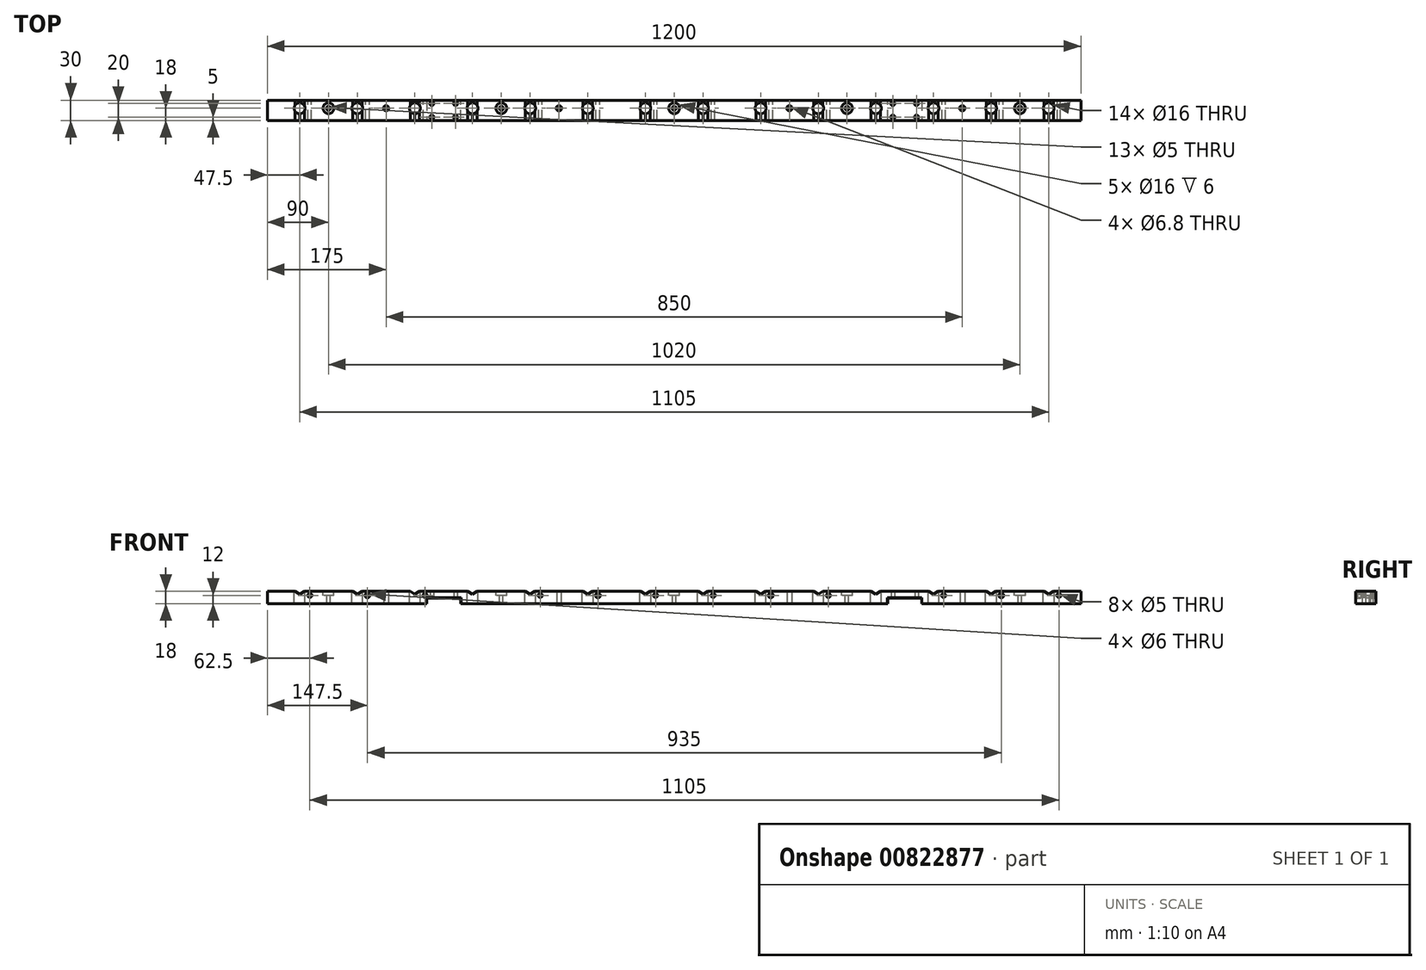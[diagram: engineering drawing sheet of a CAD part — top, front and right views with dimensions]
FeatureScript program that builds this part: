
annotation { "Feature Type Name" : "Feature", "Feature Type Description" : "" }
export const myFeature = defineFeature(function(context is Context, id is Id, definition is map)
    precondition{}
    {
        {
            var Q0;
            Q0=qCreatedBy(makeId("Front.planeOp"),FACE);
            var sketch = newSketch(context, id + "F0", { "sketchPlane" : qUnion([Q0])});
            skLineSegment(sketch, "E0.bottom", {"start": v(-600, -9) * mm, "end": v(600, -9) * mm});
            skLineSegment(sketch, "E0.top", {"start": v(-600, 9) * mm, "end": v(-559.43, 9) * mm});
            skLineSegment(sketch, "E0.left", {"start": v(-600, -9) * mm, "end": v(-600, 9) * mm});
            skLineSegment(sketch, "E0.right", {"start": v(600, -9) * mm, "end": v(600, 9) * mm});
            skPoint(sketch, "E0.middle", {"position": v(0, 0) * mm});
            skLineSegment(sketch, "E1", {"start": v(0, 0) * mm, "end": v(0, 102.74) * mm, "construction": true});
            skLineSegment(sketch, "E2", {"start": v(0, 102.74) * mm, "end": v(-552.5, 102.74) * mm, "construction": true});
            skLineSegment(sketch, "E3", {"start": v(-552.5, 102.74) * mm, "end": v(-552.5, -48.6) * mm, "construction": true});
            skLineSegment(sketch, "E4", {"start": v(-552.5, 5) * mm, "end": v(-545.57, 9) * mm});
            skLineSegment(sketch, "E5.MirrorCS", {"start": v(-552.5, 5) * mm, "end": v(-559.43, 9) * mm});
            skLineSegment(sketch, "E6.1.0.0", {"start": v(-467.5, 5) * mm, "end": v(-460.57, 9) * mm});
            skLineSegment(sketch, "E6.1.0.1", {"start": v(-467.5, 5) * mm, "end": v(-474.43, 9) * mm});
            skLineSegment(sketch, "E6.2.0.0", {"start": v(-382.5, 5) * mm, "end": v(-375.57, 9) * mm});
            skLineSegment(sketch, "E6.2.0.1", {"start": v(-382.5, 5) * mm, "end": v(-389.43, 9) * mm});
            skLineSegment(sketch, "E6.3.0.0", {"start": v(-297.5, 5) * mm, "end": v(-290.57, 9) * mm});
            skLineSegment(sketch, "E6.3.0.1", {"start": v(-297.5, 5) * mm, "end": v(-304.43, 9) * mm});
            skLineSegment(sketch, "E6.4.0.0", {"start": v(-212.5, 5) * mm, "end": v(-205.57, 9) * mm});
            skLineSegment(sketch, "E6.4.0.1", {"start": v(-212.5, 5) * mm, "end": v(-219.43, 9) * mm});
            skLineSegment(sketch, "E6.5.0.0", {"start": v(-127.5, 5) * mm, "end": v(-120.57, 9) * mm});
            skLineSegment(sketch, "E6.5.0.1", {"start": v(-127.5, 5) * mm, "end": v(-134.43, 9) * mm});
            skLineSegment(sketch, "E6.6.0.0", {"start": v(-42.5, 5) * mm, "end": v(-35.57, 9) * mm});
            skLineSegment(sketch, "E6.6.0.1", {"start": v(-42.5, 5) * mm, "end": v(-49.43, 9) * mm});
            skLineSegment(sketch, "E6.7.0.0", {"start": v(42.5, 5) * mm, "end": v(49.43, 9) * mm});
            skLineSegment(sketch, "E6.7.0.1", {"start": v(42.5, 5) * mm, "end": v(35.57, 9) * mm});
            skLineSegment(sketch, "E6.8.0.0", {"start": v(127.5, 5) * mm, "end": v(134.43, 9) * mm});
            skLineSegment(sketch, "E6.8.0.1", {"start": v(127.5, 5) * mm, "end": v(120.57, 9) * mm});
            skLineSegment(sketch, "E6.9.0.0", {"start": v(212.5, 5) * mm, "end": v(219.43, 9) * mm});
            skLineSegment(sketch, "E6.9.0.1", {"start": v(212.5, 5) * mm, "end": v(205.57, 9) * mm});
            skLineSegment(sketch, "E6.10.0.0", {"start": v(297.5, 5) * mm, "end": v(304.43, 9) * mm});
            skLineSegment(sketch, "E6.10.0.1", {"start": v(297.5, 5) * mm, "end": v(290.57, 9) * mm});
            skLineSegment(sketch, "E6.11.0.0", {"start": v(382.5, 5) * mm, "end": v(389.43, 9) * mm});
            skLineSegment(sketch, "E6.11.0.1", {"start": v(382.5, 5) * mm, "end": v(375.57, 9) * mm});
            skLineSegment(sketch, "E6.12.0.0", {"start": v(467.5, 5) * mm, "end": v(474.43, 9) * mm});
            skLineSegment(sketch, "E6.12.0.1", {"start": v(467.5, 5) * mm, "end": v(460.57, 9) * mm});
            skLineSegment(sketch, "E6.13.0.0", {"start": v(552.5, 5) * mm, "end": v(559.43, 9) * mm});
            skLineSegment(sketch, "E6.13.0.1", {"start": v(552.5, 5) * mm, "end": v(545.57, 9) * mm});
            skLineSegment(sketch, "E7.trimOffspring", {"start": v(-545.57, 9) * mm, "end": v(-474.43, 9) * mm, "construction": true});
            skLineSegment(sketch, "E8.trimOffspring", {"start": v(-460.57, 9) * mm, "end": v(-389.43, 9) * mm});
            skLineSegment(sketch, "E9.trimOffspring", {"start": v(-545.57, 9) * mm, "end": v(-474.43, 9) * mm});
            skLineSegment(sketch, "E10.trimOffspring", {"start": v(-375.57, 9) * mm, "end": v(-304.43, 9) * mm});
            skLineSegment(sketch, "E11.trimOffspring", {"start": v(-290.57, 9) * mm, "end": v(-219.43, 9) * mm});
            skLineSegment(sketch, "E12.trimOffspring", {"start": v(-205.57, 9) * mm, "end": v(-134.43, 9) * mm});
            skLineSegment(sketch, "E13.trimOffspring", {"start": v(-120.57, 9) * mm, "end": v(-49.43, 9) * mm});
            skLineSegment(sketch, "E14.trimOffspring", {"start": v(-35.57, 9) * mm, "end": v(35.57, 9) * mm});
            skLineSegment(sketch, "E15.trimOffspring", {"start": v(49.43, 9) * mm, "end": v(120.57, 9) * mm});
            skLineSegment(sketch, "E16.trimOffspring", {"start": v(134.43, 9) * mm, "end": v(205.57, 9) * mm});
            skLineSegment(sketch, "E17.trimOffspring", {"start": v(219.43, 9) * mm, "end": v(290.57, 9) * mm});
            skLineSegment(sketch, "E18.trimOffspring", {"start": v(304.43, 9) * mm, "end": v(375.57, 9) * mm});
            skLineSegment(sketch, "E19.trimOffspring", {"start": v(389.43, 9) * mm, "end": v(460.57, 9) * mm});
            skLineSegment(sketch, "E20.trimOffspring", {"start": v(474.43, 9) * mm, "end": v(545.57, 9) * mm});
            skLineSegment(sketch, "E21.trimOffspring", {"start": v(559.43, 9) * mm, "end": v(600, 9) * mm});
            skSolve(sketch);
        }
        {
            var Q0;
            Q0 = qSketchRegion(id + "F0", true);
            extrude(context, id + "F1", {"entities" : qUnion([Q0]), "endBound" : BoundingType.SYMMETRIC, "depth" : 24 * mm, "offsetDistance" : 25 * mm});
        }
        {
            var Q0;
            Q0=qCreatedBy(makeId("Top.planeOp"),FACE);
            var sketch = newSketch(context, id + "F2", { "sketchPlane" : qUnion([Q0])});
            skLineSegment(sketch, "E22", {"start": v(0, 0) * mm, "end": v(0, 120.86) * mm, "construction": true});
            skLineSegment(sketch, "E23", {"start": v(0, 120.86) * mm, "end": v(-552.5, 120.86) * mm, "construction": true});
            skLineSegment(sketch, "E24", {"start": v(-552.5, 120.86) * mm, "end": v(-552.5, 0) * mm, "construction": true});
            skLineSegment(sketch, "E25", {"start": v(0, 0) * mm, "end": v(-552.5, 0) * mm, "construction": true});
            skCircle(sketch, "E26", {"center": v(-552.5, 0) * mm, "radius": 8 * mm});
            skCircle(sketch, "E27.1.0.0", {"center": v(-467.5, 0) * mm, "radius": 8 * mm});
            skCircle(sketch, "E27.2.0.0", {"center": v(-382.5, 0) * mm, "radius": 8 * mm});
            skCircle(sketch, "E27.3.0.0", {"center": v(-297.5, 0) * mm, "radius": 8 * mm});
            skCircle(sketch, "E27.4.0.0", {"center": v(-212.5, 0) * mm, "radius": 8 * mm});
            skCircle(sketch, "E27.5.0.0", {"center": v(-127.5, 0) * mm, "radius": 8 * mm});
            skCircle(sketch, "E27.6.0.0", {"center": v(-42.5, 0) * mm, "radius": 8 * mm});
            skCircle(sketch, "E27.7.0.0", {"center": v(42.5, 0) * mm, "radius": 8 * mm});
            skCircle(sketch, "E27.8.0.0", {"center": v(127.5, 0) * mm, "radius": 8 * mm});
            skCircle(sketch, "E27.9.0.0", {"center": v(212.5, 0) * mm, "radius": 8 * mm});
            skCircle(sketch, "E27.10.0.0", {"center": v(297.5, 0) * mm, "radius": 8 * mm});
            skCircle(sketch, "E27.11.0.0", {"center": v(382.5, 0) * mm, "radius": 8 * mm});
            skCircle(sketch, "E27.12.0.0", {"center": v(467.5, 0) * mm, "radius": 8 * mm});
            skCircle(sketch, "E27.13.0.0", {"center": v(552.5, 0) * mm, "radius": 8 * mm});
            skLineSegment(sketch, "E27.direction1", {"start": v(-552.5, 0) * mm, "end": v(-467.5, 0) * mm, "construction": true});
            skSolve(sketch);
        }
        {
            var Q0;
            Q0 = qSketchRegion(id + "F2", true);
            extrude(context, id + "F3", {"entities" : qUnion([Q0]), "operationType" : NewBodyOperationType.REMOVE, "endBound" : BoundingType.SYMMETRIC, "oppositeDirection" : true, "depth" : 25 * mm, "offsetDistance" : 25 * mm});
        }
        {
            var Q0;
            Q0=makeQuery(id+"F1.opExtrude","CAP_FACE",FACE,{"disambiguationData":[OSD([sQuery(id+"F0.wireOp",EDGE,"E0.bottom"),sQuery(id+"F0.wireOp",EDGE,"E0.top"),sQuery(id+"F0.wireOp",EDGE,"E0.left"),sQuery(id+"F0.wireOp",EDGE,"E0.right"),sQuery(id+"F0.wireOp",EDGE,"E4"),sQuery(id+"F0.wireOp",EDGE,"E5.MirrorCS"),sQuery(id+"F0.wireOp",EDGE,"E6.1.0.0"),sQuery(id+"F0.wireOp",EDGE,"E6.1.0.1"),sQuery(id+"F0.wireOp",EDGE,"E6.2.0.0"),sQuery(id+"F0.wireOp",EDGE,"E6.2.0.1"),sQuery(id+"F0.wireOp",EDGE,"E6.3.0.0"),sQuery(id+"F0.wireOp",EDGE,"E6.3.0.1"),sQuery(id+"F0.wireOp",EDGE,"E6.4.0.0"),sQuery(id+"F0.wireOp",EDGE,"E6.4.0.1"),sQuery(id+"F0.wireOp",EDGE,"E6.5.0.0"),sQuery(id+"F0.wireOp",EDGE,"E6.5.0.1"),sQuery(id+"F0.wireOp",EDGE,"E6.6.0.0"),sQuery(id+"F0.wireOp",EDGE,"E6.6.0.1"),sQuery(id+"F0.wireOp",EDGE,"E6.7.0.0"),sQuery(id+"F0.wireOp",EDGE,"E6.7.0.1"),sQuery(id+"F0.wireOp",EDGE,"E6.8.0.0"),sQuery(id+"F0.wireOp",EDGE,"E6.8.0.1"),sQuery(id+"F0.wireOp",EDGE,"E6.9.0.0"),sQuery(id+"F0.wireOp",EDGE,"E6.9.0.1"),sQuery(id+"F0.wireOp",EDGE,"E6.10.0.0"),sQuery(id+"F0.wireOp",EDGE,"E6.10.0.1"),sQuery(id+"F0.wireOp",EDGE,"E6.11.0.0"),sQuery(id+"F0.wireOp",EDGE,"E6.11.0.1"),sQuery(id+"F0.wireOp",EDGE,"E6.12.0.0"),sQuery(id+"F0.wireOp",EDGE,"E6.12.0.1"),sQuery(id+"F0.wireOp",EDGE,"E6.13.0.0"),sQuery(id+"F0.wireOp",EDGE,"E6.13.0.1"),sQuery(id+"F0.wireOp",EDGE,"E8.trimOffspring"),sQuery(id+"F0.wireOp",EDGE,"E9.trimOffspring"),sQuery(id+"F0.wireOp",EDGE,"E10.trimOffspring"),sQuery(id+"F0.wireOp",EDGE,"E11.trimOffspring"),sQuery(id+"F0.wireOp",EDGE,"E12.trimOffspring"),sQuery(id+"F0.wireOp",EDGE,"E13.trimOffspring"),sQuery(id+"F0.wireOp",EDGE,"E14.trimOffspring"),sQuery(id+"F0.wireOp",EDGE,"E15.trimOffspring"),sQuery(id+"F0.wireOp",EDGE,"E16.trimOffspring"),sQuery(id+"F0.wireOp",EDGE,"E17.trimOffspring"),sQuery(id+"F0.wireOp",EDGE,"E18.trimOffspring"),sQuery(id+"F0.wireOp",EDGE,"E19.trimOffspring"),sQuery(id+"F0.wireOp",EDGE,"E20.trimOffspring"),sQuery(id+"F0.wireOp",EDGE,"E21.trimOffspring")])],"isStart":false});
            extrude(context, id + "F4", {"entities" : qUnion([Q0]), "operationType" : NewBodyOperationType.ADD, "depth" : 6 * mm, "offsetDistance" : 25 * mm});
        }
        {
            var Q0;
            Q0=makeQuery(id+"F1.opExtrude","CAP_FACE",FACE,{"disambiguationData":[OSD([sQuery(id+"F0.wireOp",EDGE,"E0.bottom"),sQuery(id+"F0.wireOp",EDGE,"E0.top"),sQuery(id+"F0.wireOp",EDGE,"E0.left"),sQuery(id+"F0.wireOp",EDGE,"E0.right"),sQuery(id+"F0.wireOp",EDGE,"E4"),sQuery(id+"F0.wireOp",EDGE,"E5.MirrorCS"),sQuery(id+"F0.wireOp",EDGE,"E6.1.0.0"),sQuery(id+"F0.wireOp",EDGE,"E6.1.0.1"),sQuery(id+"F0.wireOp",EDGE,"E6.2.0.0"),sQuery(id+"F0.wireOp",EDGE,"E6.2.0.1"),sQuery(id+"F0.wireOp",EDGE,"E6.3.0.0"),sQuery(id+"F0.wireOp",EDGE,"E6.3.0.1"),sQuery(id+"F0.wireOp",EDGE,"E6.4.0.0"),sQuery(id+"F0.wireOp",EDGE,"E6.4.0.1"),sQuery(id+"F0.wireOp",EDGE,"E6.5.0.0"),sQuery(id+"F0.wireOp",EDGE,"E6.5.0.1"),sQuery(id+"F0.wireOp",EDGE,"E6.6.0.0"),sQuery(id+"F0.wireOp",EDGE,"E6.6.0.1"),sQuery(id+"F0.wireOp",EDGE,"E6.7.0.0"),sQuery(id+"F0.wireOp",EDGE,"E6.7.0.1"),sQuery(id+"F0.wireOp",EDGE,"E6.8.0.0"),sQuery(id+"F0.wireOp",EDGE,"E6.8.0.1"),sQuery(id+"F0.wireOp",EDGE,"E6.9.0.0"),sQuery(id+"F0.wireOp",EDGE,"E6.9.0.1"),sQuery(id+"F0.wireOp",EDGE,"E6.10.0.0"),sQuery(id+"F0.wireOp",EDGE,"E6.10.0.1"),sQuery(id+"F0.wireOp",EDGE,"E6.11.0.0"),sQuery(id+"F0.wireOp",EDGE,"E6.11.0.1"),sQuery(id+"F0.wireOp",EDGE,"E6.12.0.0"),sQuery(id+"F0.wireOp",EDGE,"E6.12.0.1"),sQuery(id+"F0.wireOp",EDGE,"E6.13.0.0"),sQuery(id+"F0.wireOp",EDGE,"E6.13.0.1"),sQuery(id+"F0.wireOp",EDGE,"E8.trimOffspring"),sQuery(id+"F0.wireOp",EDGE,"E9.trimOffspring"),sQuery(id+"F0.wireOp",EDGE,"E10.trimOffspring"),sQuery(id+"F0.wireOp",EDGE,"E11.trimOffspring"),sQuery(id+"F0.wireOp",EDGE,"E12.trimOffspring"),sQuery(id+"F0.wireOp",EDGE,"E13.trimOffspring"),sQuery(id+"F0.wireOp",EDGE,"E14.trimOffspring"),sQuery(id+"F0.wireOp",EDGE,"E15.trimOffspring"),sQuery(id+"F0.wireOp",EDGE,"E16.trimOffspring"),sQuery(id+"F0.wireOp",EDGE,"E17.trimOffspring"),sQuery(id+"F0.wireOp",EDGE,"E18.trimOffspring"),sQuery(id+"F0.wireOp",EDGE,"E19.trimOffspring"),sQuery(id+"F0.wireOp",EDGE,"E20.trimOffspring"),sQuery(id+"F0.wireOp",EDGE,"E21.trimOffspring")])],"isStart":true});
            var sketch = newSketch(context, id + "F5", { "sketchPlane" : qUnion([Q0])});
            skLineSegment(sketch, "E28.0", {"start": v(-559.43, 9) * mm, "end": v(-600, 9) * mm, "construction": true});
            skLineSegment(sketch, "E29", {"start": v(-631.78, 3) * mm, "end": v(-527.52, 3) * mm, "construction": true});
            skLineSegment(sketch, "E30", {"start": v(-527.52, 3) * mm, "end": v(-567.5, 61.8) * mm, "construction": true});
            skLineSegment(sketch, "E31", {"start": v(-567.5, 61.8) * mm, "end": v(-567.5, -52.53) * mm, "construction": true});
            skCircle(sketch, "E32", {"center": v(-567.5, 3) * mm, "radius": 2.5 * mm});
            skCircle(sketch, "E33.1.0.0", {"center": v(-482.5, 3) * mm, "radius": 2.5 * mm, "construction": true});
            skCircle(sketch, "E33.2.0.0", {"center": v(-397.5, 3) * mm, "radius": 2.5 * mm});
            skCircle(sketch, "E33.3.0.0", {"center": v(-312.5, 3) * mm, "radius": 2.5 * mm, "construction": true});
            skCircle(sketch, "E33.4.0.0", {"center": v(-227.5, 3) * mm, "radius": 2.5 * mm});
            skCircle(sketch, "E33.5.0.0", {"center": v(-142.5, 3) * mm, "radius": 2.5 * mm, "construction": true});
            skCircle(sketch, "E33.6.0.0", {"center": v(-57.5, 3) * mm, "radius": 2.5 * mm});
            skCircle(sketch, "E33.7.0.0", {"center": v(27.5, 3) * mm, "radius": 2.5 * mm});
            skCircle(sketch, "E33.8.0.0", {"center": v(112.5, 3) * mm, "radius": 2.5 * mm, "construction": true});
            skCircle(sketch, "E33.9.0.0", {"center": v(197.5, 3) * mm, "radius": 2.5 * mm});
            skCircle(sketch, "E33.10.0.0", {"center": v(282.5, 3) * mm, "radius": 2.5 * mm, "construction": true});
            skCircle(sketch, "E33.11.0.0", {"center": v(367.5, 3) * mm, "radius": 2.5 * mm});
            skCircle(sketch, "E33.12.0.0", {"center": v(452.5, 3) * mm, "radius": 2.5 * mm, "construction": true});
            skCircle(sketch, "E33.13.0.0", {"center": v(537.5, 3) * mm, "radius": 2.5 * mm});
            skLineSegment(sketch, "E33.direction1", {"start": v(-567.5, 3) * mm, "end": v(-482.5, 3) * mm, "construction": true});
            skSolve(sketch);
        }
        {
            var Q0;
            Q0 = qSketchRegion(id + "F5", true);
            extrude(context, id + "F6", {"entities" : qUnion([Q0]), "operationType" : NewBodyOperationType.REMOVE, "endBound" : BoundingType.UP_TO_NEXT, "oppositeDirection" : true, "depth" : 15 * mm, "offsetDistance" : 25 * mm});
        }
        {
            var Q0;
            Q0=makeQuery(id+"F5.imprint","IMPRINT",FACE,{"disambiguationData":[TD([[makeQuery(id+"F5.imprint","IMPRINT",EDGE,{"derivedFrom":sQuery(id+"F5.wireOp",EDGE,"E32")}),-1.0]])]});
            var sketch = newSketch(context, id + "F7", { "sketchPlane" : qUnion([Q0])});
            skCircle(sketch, "E34.0", {"center": v(-482.5, 3) * mm, "radius": 2.5 * mm, "construction": true});
            skCircle(sketch, "E35.0", {"center": v(-142.5, 3) * mm, "radius": 2.5 * mm, "construction": true});
            skCircle(sketch, "E36.0", {"center": v(112.5, 3) * mm, "radius": 2.5 * mm, "construction": true});
            skCircle(sketch, "E37.0", {"center": v(452.5, 3) * mm, "radius": 2.5 * mm, "construction": true});
            skCircle(sketch, "E38", {"center": v(-482.5, 3) * mm, "radius": 3 * mm});
            skCircle(sketch, "E39", {"center": v(-142.5, 3) * mm, "radius": 3 * mm});
            skCircle(sketch, "E40", {"center": v(112.5, 3) * mm, "radius": 3 * mm});
            skCircle(sketch, "E41", {"center": v(452.5, 3) * mm, "radius": 3 * mm});
            skSolve(sketch);
        }
        {
            var Q0;
            Q0 = qSketchRegion(id + "F7", true);
            extrude(context, id + "F8", {"entities" : qUnion([Q0]), "operationType" : NewBodyOperationType.REMOVE, "endBound" : BoundingType.UP_TO_NEXT, "oppositeDirection" : true, "depth" : 25 * mm, "offsetDistance" : 25 * mm});
        }
        {
            var Q0;
            Q0=makeQuery(id+"F6.boolean.opBoolean","COPY",FACE,{"derivedFrom":makeQuery(id+"F6.opExtrude","SWEPT_FACE",FACE,{"disambiguationData":[OSD([sQuery(id+"F5.wireOp",EDGE,"E32")])]})});
            var Q1;
            Q1=makeQuery(id+"F8.boolean.opBoolean","COPY",FACE,{"derivedFrom":makeQuery(id+"F8.opExtrude","SWEPT_FACE",FACE,{"disambiguationData":[OSD([sQuery(id+"F7.wireOp",EDGE,"E38")])]})});
            var Q2;
            Q2=makeQuery(id+"F6.boolean.opBoolean","COPY",FACE,{"derivedFrom":makeQuery(id+"F6.opExtrude","SWEPT_FACE",FACE,{"disambiguationData":[OSD([sQuery(id+"F5.wireOp",EDGE,"E33.2.0.0")])]})});
            var Q3;
            Q3=makeQuery(id+"F6.boolean.opBoolean","COPY",FACE,{"derivedFrom":makeQuery(id+"F6.opExtrude","SWEPT_FACE",FACE,{"disambiguationData":[OSD([sQuery(id+"F5.wireOp",EDGE,"E33.4.0.0")])]})});
            var Q4;
            Q4=makeQuery(id+"F8.boolean.opBoolean","COPY",FACE,{"derivedFrom":makeQuery(id+"F8.opExtrude","SWEPT_FACE",FACE,{"disambiguationData":[OSD([sQuery(id+"F7.wireOp",EDGE,"E39")])]})});
            var Q5;
            Q5=makeQuery(id+"F6.boolean.opBoolean","COPY",FACE,{"derivedFrom":makeQuery(id+"F6.opExtrude","SWEPT_FACE",FACE,{"disambiguationData":[OSD([sQuery(id+"F5.wireOp",EDGE,"E33.6.0.0")])]})});
            var Q6;
            Q6=makeQuery(id+"F6.boolean.opBoolean","COPY",FACE,{"derivedFrom":makeQuery(id+"F6.opExtrude","SWEPT_FACE",FACE,{"disambiguationData":[OSD([sQuery(id+"F5.wireOp",EDGE,"E33.7.0.0")])]})});
            var Q7;
            Q7=makeQuery(id+"F8.boolean.opBoolean","COPY",FACE,{"derivedFrom":makeQuery(id+"F8.opExtrude","SWEPT_FACE",FACE,{"disambiguationData":[OSD([sQuery(id+"F7.wireOp",EDGE,"E40")])]})});
            var Q8;
            Q8=makeQuery(id+"F6.boolean.opBoolean","COPY",FACE,{"derivedFrom":makeQuery(id+"F6.opExtrude","SWEPT_FACE",FACE,{"disambiguationData":[OSD([sQuery(id+"F5.wireOp",EDGE,"E33.9.0.0")])]})});
            var Q9;
            Q9=makeQuery(id+"F6.boolean.opBoolean","COPY",FACE,{"derivedFrom":makeQuery(id+"F6.opExtrude","SWEPT_FACE",FACE,{"disambiguationData":[OSD([sQuery(id+"F5.wireOp",EDGE,"E33.11.0.0")])]})});
            var Q10;
            Q10=makeQuery(id+"F8.boolean.opBoolean","COPY",FACE,{"derivedFrom":makeQuery(id+"F8.opExtrude","SWEPT_FACE",FACE,{"disambiguationData":[OSD([sQuery(id+"F7.wireOp",EDGE,"E41")])]})});
            var Q11;
            Q11=makeQuery(id+"F6.boolean.opBoolean","COPY",FACE,{"derivedFrom":makeQuery(id+"F6.opExtrude","SWEPT_FACE",FACE,{"disambiguationData":[OSD([sQuery(id+"F5.wireOp",EDGE,"E33.13.0.0")])]})});
            var Q12;
            Q12=makeQuery(id+"F3.boolean.opBoolean","INTERSECT",EDGE,{"derivedFrom":[makeQuery(id+"F1.opExtrude","SWEPT_FACE",FACE,{"disambiguationData":[OSD([sQuery(id+"F0.wireOp",EDGE,"E0.bottom")])]}),makeQuery(id+"F3.opExtrude","SWEPT_FACE",FACE,{"disambiguationData":[OSD([sQuery(id+"F2.wireOp",EDGE,"E26")])]})]});
            var Q13;
            Q13=makeQuery(id+"F3.boolean.opBoolean","INTERSECT",EDGE,{"derivedFrom":[makeQuery(id+"F1.opExtrude","SWEPT_FACE",FACE,{"disambiguationData":[OSD([sQuery(id+"F0.wireOp",EDGE,"E0.bottom")])]}),makeQuery(id+"F3.opExtrude","SWEPT_FACE",FACE,{"disambiguationData":[OSD([sQuery(id+"F2.wireOp",EDGE,"E27.1.0.0")])]})]});
            var Q14;
            Q14=makeQuery(id+"F3.boolean.opBoolean","INTERSECT",EDGE,{"derivedFrom":[makeQuery(id+"F1.opExtrude","SWEPT_FACE",FACE,{"disambiguationData":[OSD([sQuery(id+"F0.wireOp",EDGE,"E0.bottom")])]}),makeQuery(id+"F3.opExtrude","SWEPT_FACE",FACE,{"disambiguationData":[OSD([sQuery(id+"F2.wireOp",EDGE,"E27.2.0.0")])]})]});
            var Q15;
            Q15=makeQuery(id+"F3.boolean.opBoolean","INTERSECT",EDGE,{"derivedFrom":[makeQuery(id+"F1.opExtrude","SWEPT_FACE",FACE,{"disambiguationData":[OSD([sQuery(id+"F0.wireOp",EDGE,"E0.bottom")])]}),makeQuery(id+"F3.opExtrude","SWEPT_FACE",FACE,{"disambiguationData":[OSD([sQuery(id+"F2.wireOp",EDGE,"E27.3.0.0")])]})]});
            var Q16;
            Q16=makeQuery(id+"F3.boolean.opBoolean","INTERSECT",EDGE,{"derivedFrom":[makeQuery(id+"F1.opExtrude","SWEPT_FACE",FACE,{"disambiguationData":[OSD([sQuery(id+"F0.wireOp",EDGE,"E0.bottom")])]}),makeQuery(id+"F3.opExtrude","SWEPT_FACE",FACE,{"disambiguationData":[OSD([sQuery(id+"F2.wireOp",EDGE,"E27.4.0.0")])]})]});
            var Q17;
            Q17=makeQuery(id+"F3.boolean.opBoolean","INTERSECT",EDGE,{"derivedFrom":[makeQuery(id+"F1.opExtrude","SWEPT_FACE",FACE,{"disambiguationData":[OSD([sQuery(id+"F0.wireOp",EDGE,"E0.bottom")])]}),makeQuery(id+"F3.opExtrude","SWEPT_FACE",FACE,{"disambiguationData":[OSD([sQuery(id+"F2.wireOp",EDGE,"E27.5.0.0")])]})]});
            var Q18;
            Q18=makeQuery(id+"F3.boolean.opBoolean","INTERSECT",EDGE,{"derivedFrom":[makeQuery(id+"F1.opExtrude","SWEPT_FACE",FACE,{"disambiguationData":[OSD([sQuery(id+"F0.wireOp",EDGE,"E0.bottom")])]}),makeQuery(id+"F3.opExtrude","SWEPT_FACE",FACE,{"disambiguationData":[OSD([sQuery(id+"F2.wireOp",EDGE,"E27.6.0.0")])]})]});
            var Q19;
            Q19=makeQuery(id+"F3.boolean.opBoolean","INTERSECT",EDGE,{"derivedFrom":[makeQuery(id+"F1.opExtrude","SWEPT_FACE",FACE,{"disambiguationData":[OSD([sQuery(id+"F0.wireOp",EDGE,"E0.bottom")])]}),makeQuery(id+"F3.opExtrude","SWEPT_FACE",FACE,{"disambiguationData":[OSD([sQuery(id+"F2.wireOp",EDGE,"E27.7.0.0")])]})]});
            var Q20;
            Q20=makeQuery(id+"F3.boolean.opBoolean","INTERSECT",EDGE,{"derivedFrom":[makeQuery(id+"F1.opExtrude","SWEPT_FACE",FACE,{"disambiguationData":[OSD([sQuery(id+"F0.wireOp",EDGE,"E0.bottom")])]}),makeQuery(id+"F3.opExtrude","SWEPT_FACE",FACE,{"disambiguationData":[OSD([sQuery(id+"F2.wireOp",EDGE,"E27.8.0.0")])]})]});
            var Q21;
            Q21=makeQuery(id+"F3.boolean.opBoolean","INTERSECT",EDGE,{"derivedFrom":[makeQuery(id+"F1.opExtrude","SWEPT_FACE",FACE,{"disambiguationData":[OSD([sQuery(id+"F0.wireOp",EDGE,"E0.bottom")])]}),makeQuery(id+"F3.opExtrude","SWEPT_FACE",FACE,{"disambiguationData":[OSD([sQuery(id+"F2.wireOp",EDGE,"E27.9.0.0")])]})]});
            var Q22;
            Q22=makeQuery(id+"F3.boolean.opBoolean","INTERSECT",EDGE,{"derivedFrom":[makeQuery(id+"F1.opExtrude","SWEPT_FACE",FACE,{"disambiguationData":[OSD([sQuery(id+"F0.wireOp",EDGE,"E0.bottom")])]}),makeQuery(id+"F3.opExtrude","SWEPT_FACE",FACE,{"disambiguationData":[OSD([sQuery(id+"F2.wireOp",EDGE,"E27.10.0.0")])]})]});
            var Q23;
            Q23=makeQuery(id+"F3.boolean.opBoolean","INTERSECT",EDGE,{"derivedFrom":[makeQuery(id+"F1.opExtrude","SWEPT_FACE",FACE,{"disambiguationData":[OSD([sQuery(id+"F0.wireOp",EDGE,"E0.bottom")])]}),makeQuery(id+"F3.opExtrude","SWEPT_FACE",FACE,{"disambiguationData":[OSD([sQuery(id+"F2.wireOp",EDGE,"E27.11.0.0")])]})]});
            var Q24;
            Q24=makeQuery(id+"F3.boolean.opBoolean","INTERSECT",EDGE,{"derivedFrom":[makeQuery(id+"F1.opExtrude","SWEPT_FACE",FACE,{"disambiguationData":[OSD([sQuery(id+"F0.wireOp",EDGE,"E0.bottom")])]}),makeQuery(id+"F3.opExtrude","SWEPT_FACE",FACE,{"disambiguationData":[OSD([sQuery(id+"F2.wireOp",EDGE,"E27.12.0.0")])]})]});
            var Q25;
            Q25=makeQuery(id+"F3.boolean.opBoolean","INTERSECT",EDGE,{"derivedFrom":[makeQuery(id+"F1.opExtrude","SWEPT_FACE",FACE,{"disambiguationData":[OSD([sQuery(id+"F0.wireOp",EDGE,"E0.bottom")])]}),makeQuery(id+"F3.opExtrude","SWEPT_FACE",FACE,{"disambiguationData":[OSD([sQuery(id+"F2.wireOp",EDGE,"E27.13.0.0")])]})]});
            chamfer(context, id + "F9", {"entities" : qUnion([Q0, Q1, Q2, Q3, Q4, Q5, Q6, Q7, Q8, Q9, Q10, Q11, Q12, Q13, Q14, Q15, Q16, Q17, Q18, Q19, Q20, Q21, Q22, Q23, Q24, Q25]), "width" : 0.5 * mm, "tangentPropagation" : true});
        }
        {
            var Q0;
            Q0=qCreatedBy(makeId("Top.planeOp"),FACE);
            var sketch = newSketch(context, id + "F10", { "sketchPlane" : qUnion([Q0])});
            skLineSegment(sketch, "E42", {"start": v(0, 0) * mm, "end": v(-510, 0) * mm, "construction": true});
            skCircle(sketch, "E43", {"center": v(-510, 0) * mm, "radius": 2.5 * mm});
            skCircle(sketch, "E44", {"center": v(-510, 0) * mm, "radius": 8 * mm, "construction": true});
            skCircle(sketch, "E45.1.0.0", {"center": v(-255, 0) * mm, "radius": 2.5 * mm});
            skCircle(sketch, "E45.2.0.0", {"center": v(0, 0) * mm, "radius": 2.5 * mm});
            skCircle(sketch, "E45.3.0.0", {"center": v(255, 0) * mm, "radius": 2.5 * mm});
            skCircle(sketch, "E45.4.0.0", {"center": v(510, 0) * mm, "radius": 2.5 * mm});
            skLineSegment(sketch, "E45.direction1", {"start": v(-510, 0) * mm, "end": v(-255, 0) * mm, "construction": true});
            skSolve(sketch);
        }
        {
            var Q0;
            Q0 = qSketchRegion(id + "F10", true);
            extrude(context, id + "F11", {"entities" : qUnion([Q0]), "operationType" : NewBodyOperationType.REMOVE, "endBound" : BoundingType.SYMMETRIC, "oppositeDirection" : true, "depth" : 25 * mm, "offsetDistance" : 25 * mm});
        }
        {
            var Q0;
            {var subQ0=sQuery(id+"F0.wireOp",EDGE,"E9.trimOffspring");Q0=makeQuery(id+"F4.boolean.opBoolean","MERGE",FACE,{"derivedFrom":[makeQuery(id+"F1.opExtrude","SWEPT_FACE",FACE,{"disambiguationData":[OSD([subQ0])]}),makeQuery(id+"F4.opExtrude","SWEPT_FACE",FACE,{"disambiguationData":[OSD([subQ0])]})]});}
            var sketch = newSketch(context, id + "F12", { "sketchPlane" : qUnion([Q0])});
            skCircle(sketch, "E46.0", {"center": v(-510, 0) * mm, "radius": 2.5 * mm, "construction": true});
            skCircle(sketch, "E47.0", {"center": v(-255, 0) * mm, "radius": 2.5 * mm, "construction": true});
            skCircle(sketch, "E48.0", {"center": v(0, 0) * mm, "radius": 2.5 * mm, "construction": true});
            skCircle(sketch, "E49.0", {"center": v(255, 0) * mm, "radius": 2.5 * mm, "construction": true});
            skCircle(sketch, "E50.0", {"center": v(510, 0) * mm, "radius": 2.5 * mm, "construction": true});
            skCircle(sketch, "E51", {"center": v(-510, 0) * mm, "radius": 8 * mm});
            skCircle(sketch, "E52.1.0.0", {"center": v(-255, 0) * mm, "radius": 8 * mm});
            skCircle(sketch, "E52.2.0.0", {"center": v(0, 0) * mm, "radius": 8 * mm});
            skCircle(sketch, "E52.3.0.0", {"center": v(255, 0) * mm, "radius": 8 * mm});
            skCircle(sketch, "E52.4.0.0", {"center": v(510, 0) * mm, "radius": 8 * mm});
            skLineSegment(sketch, "E52.direction1", {"start": v(-510, 0) * mm, "end": v(-255, 0) * mm, "construction": true});
            skSolve(sketch);
        }
        {
            var Q0;
            Q0 = qSketchRegion(id + "F12", true);
            extrude(context, id + "F13", {"entities" : qUnion([Q0]), "operationType" : NewBodyOperationType.REMOVE, "oppositeDirection" : true, "depth" : 6 * mm, "offsetDistance" : 25 * mm});
        }
        {
            var Q0;
            Q0=makeQuery(id+"F13.boolean.opBoolean","COPY",EDGE,{"derivedFrom":makeQuery(id+"F13.opExtrude","CAP_EDGE",EDGE,{"disambiguationData":[OSD([sQuery(id+"F12.wireOp",EDGE,"E52.3.0.0")])],"isStart":true})});
            var Q1;
            Q1=makeQuery(id+"F13.boolean.opBoolean","COPY",EDGE,{"derivedFrom":makeQuery(id+"F13.opExtrude","CAP_EDGE",EDGE,{"disambiguationData":[OSD([sQuery(id+"F12.wireOp",EDGE,"E52.4.0.0")])],"isStart":true})});
            var Q2;
            Q2=makeQuery(id+"F13.boolean.opBoolean","COPY",EDGE,{"derivedFrom":makeQuery(id+"F13.opExtrude","CAP_EDGE",EDGE,{"disambiguationData":[OSD([sQuery(id+"F12.wireOp",EDGE,"E52.2.0.0")])],"isStart":true})});
            var Q3;
            Q3=makeQuery(id+"F13.boolean.opBoolean","COPY",EDGE,{"derivedFrom":makeQuery(id+"F13.opExtrude","CAP_EDGE",EDGE,{"disambiguationData":[OSD([sQuery(id+"F12.wireOp",EDGE,"E52.1.0.0")])],"isStart":true})});
            var Q4;
            Q4=makeQuery(id+"F13.boolean.opBoolean","COPY",EDGE,{"derivedFrom":makeQuery(id+"F13.opExtrude","CAP_EDGE",EDGE,{"disambiguationData":[OSD([sQuery(id+"F12.wireOp",EDGE,"E51")])],"isStart":true})});
            var Q5;
            {var subQ0=sQuery(id+"F0.wireOp",EDGE,"E0.bottom");Q5=makeQuery(id+"F11.boolean.opBoolean","INTERSECT",EDGE,{"derivedFrom":[makeQuery(id+"F4.boolean.opBoolean","MERGE",FACE,{"derivedFrom":[makeQuery(id+"F1.opExtrude","SWEPT_FACE",FACE,{"disambiguationData":[OSD([subQ0])]}),makeQuery(id+"F4.opExtrude","SWEPT_FACE",FACE,{"disambiguationData":[OSD([subQ0])]})]}),makeQuery(id+"F11.opExtrude","SWEPT_FACE",FACE,{"disambiguationData":[OSD([sQuery(id+"F10.wireOp",EDGE,"E43")])]})]});}
            var Q6;
            {var subQ0=sQuery(id+"F0.wireOp",EDGE,"E0.bottom");Q6=makeQuery(id+"F11.boolean.opBoolean","INTERSECT",EDGE,{"derivedFrom":[makeQuery(id+"F4.boolean.opBoolean","MERGE",FACE,{"derivedFrom":[makeQuery(id+"F1.opExtrude","SWEPT_FACE",FACE,{"disambiguationData":[OSD([subQ0])]}),makeQuery(id+"F4.opExtrude","SWEPT_FACE",FACE,{"disambiguationData":[OSD([subQ0])]})]}),makeQuery(id+"F11.opExtrude","SWEPT_FACE",FACE,{"disambiguationData":[OSD([sQuery(id+"F10.wireOp",EDGE,"E45.1.0.0")])]})]});}
            var Q7;
            {var subQ0=sQuery(id+"F0.wireOp",EDGE,"E0.bottom");Q7=makeQuery(id+"F11.boolean.opBoolean","INTERSECT",EDGE,{"derivedFrom":[makeQuery(id+"F4.boolean.opBoolean","MERGE",FACE,{"derivedFrom":[makeQuery(id+"F1.opExtrude","SWEPT_FACE",FACE,{"disambiguationData":[OSD([subQ0])]}),makeQuery(id+"F4.opExtrude","SWEPT_FACE",FACE,{"disambiguationData":[OSD([subQ0])]})]}),makeQuery(id+"F11.opExtrude","SWEPT_FACE",FACE,{"disambiguationData":[OSD([sQuery(id+"F10.wireOp",EDGE,"E45.2.0.0")])]})]});}
            var Q8;
            {var subQ0=sQuery(id+"F0.wireOp",EDGE,"E0.bottom");Q8=makeQuery(id+"F11.boolean.opBoolean","INTERSECT",EDGE,{"derivedFrom":[makeQuery(id+"F4.boolean.opBoolean","MERGE",FACE,{"derivedFrom":[makeQuery(id+"F1.opExtrude","SWEPT_FACE",FACE,{"disambiguationData":[OSD([subQ0])]}),makeQuery(id+"F4.opExtrude","SWEPT_FACE",FACE,{"disambiguationData":[OSD([subQ0])]})]}),makeQuery(id+"F11.opExtrude","SWEPT_FACE",FACE,{"disambiguationData":[OSD([sQuery(id+"F10.wireOp",EDGE,"E45.3.0.0")])]})]});}
            var Q9;
            {var subQ0=sQuery(id+"F0.wireOp",EDGE,"E0.bottom");Q9=makeQuery(id+"F11.boolean.opBoolean","INTERSECT",EDGE,{"derivedFrom":[makeQuery(id+"F4.boolean.opBoolean","MERGE",FACE,{"derivedFrom":[makeQuery(id+"F1.opExtrude","SWEPT_FACE",FACE,{"disambiguationData":[OSD([subQ0])]}),makeQuery(id+"F4.opExtrude","SWEPT_FACE",FACE,{"disambiguationData":[OSD([subQ0])]})]}),makeQuery(id+"F11.opExtrude","SWEPT_FACE",FACE,{"disambiguationData":[OSD([sQuery(id+"F10.wireOp",EDGE,"E45.4.0.0")])]})]});}
            var Q10;
            Q10=makeQuery(id+"F13.boolean.opBoolean","INTERSECT",EDGE,{"derivedFrom":[makeQuery(id+"F11.boolean.opBoolean","COPY",FACE,{"derivedFrom":makeQuery(id+"F11.opExtrude","SWEPT_FACE",FACE,{"disambiguationData":[OSD([sQuery(id+"F10.wireOp",EDGE,"E45.4.0.0")])]})}),makeQuery(id+"F13.opExtrude","CAP_FACE",FACE,{"disambiguationData":[OSD([sQuery(id+"F12.wireOp",EDGE,"E52.4.0.0")])],"isStart":false})]});
            var Q11;
            Q11=makeQuery(id+"F13.boolean.opBoolean","INTERSECT",EDGE,{"derivedFrom":[makeQuery(id+"F11.boolean.opBoolean","COPY",FACE,{"derivedFrom":makeQuery(id+"F11.opExtrude","SWEPT_FACE",FACE,{"disambiguationData":[OSD([sQuery(id+"F10.wireOp",EDGE,"E45.3.0.0")])]})}),makeQuery(id+"F13.opExtrude","CAP_FACE",FACE,{"disambiguationData":[OSD([sQuery(id+"F12.wireOp",EDGE,"E52.3.0.0")])],"isStart":false})]});
            var Q12;
            Q12=makeQuery(id+"F13.boolean.opBoolean","INTERSECT",EDGE,{"derivedFrom":[makeQuery(id+"F11.boolean.opBoolean","COPY",FACE,{"derivedFrom":makeQuery(id+"F11.opExtrude","SWEPT_FACE",FACE,{"disambiguationData":[OSD([sQuery(id+"F10.wireOp",EDGE,"E45.2.0.0")])]})}),makeQuery(id+"F13.opExtrude","CAP_FACE",FACE,{"disambiguationData":[OSD([sQuery(id+"F12.wireOp",EDGE,"E52.2.0.0")])],"isStart":false})]});
            var Q13;
            Q13=makeQuery(id+"F13.boolean.opBoolean","INTERSECT",EDGE,{"derivedFrom":[makeQuery(id+"F11.boolean.opBoolean","COPY",FACE,{"derivedFrom":makeQuery(id+"F11.opExtrude","SWEPT_FACE",FACE,{"disambiguationData":[OSD([sQuery(id+"F10.wireOp",EDGE,"E45.1.0.0")])]})}),makeQuery(id+"F13.opExtrude","CAP_FACE",FACE,{"disambiguationData":[OSD([sQuery(id+"F12.wireOp",EDGE,"E52.1.0.0")])],"isStart":false})]});
            var Q14;
            Q14=makeQuery(id+"F13.boolean.opBoolean","INTERSECT",EDGE,{"derivedFrom":[makeQuery(id+"F11.boolean.opBoolean","COPY",FACE,{"derivedFrom":makeQuery(id+"F11.opExtrude","SWEPT_FACE",FACE,{"disambiguationData":[OSD([sQuery(id+"F10.wireOp",EDGE,"E43")])]})}),makeQuery(id+"F13.opExtrude","CAP_FACE",FACE,{"disambiguationData":[OSD([sQuery(id+"F12.wireOp",EDGE,"E51")])],"isStart":false})]});
            chamfer(context, id + "F14", {"entities" : qUnion([Q0, Q1, Q2, Q3, Q4, Q5, Q6, Q7, Q8, Q9, Q10, Q11, Q12, Q13, Q14]), "width" : .5 * mm, "tangentPropagation" : true});
        }
        {
            var Q0;
            {var subQ0=sQuery(id+"F0.wireOp",EDGE,"E0.bottom");Q0=makeQuery(id+"F4.boolean.opBoolean","MERGE",FACE,{"derivedFrom":[makeQuery(id+"F1.opExtrude","SWEPT_FACE",FACE,{"disambiguationData":[OSD([subQ0])]}),makeQuery(id+"F4.opExtrude","SWEPT_FACE",FACE,{"disambiguationData":[OSD([subQ0])]})]});}
            var sketch = newSketch(context, id + "F15", { "sketchPlane" : qUnion([Q0])});
            skLineSegment(sketch, "E53", {"start": v(0, 0) * mm, "end": v(0, -9.96) * mm, "construction": true});
            skLineSegment(sketch, "E54", {"start": v(0, 0) * mm, "end": v(-425, 0) * mm, "construction": true});
            skLineSegment(sketch, "E55", {"start": v(-425, 0) * mm, "end": v(-425, 7.63) * mm, "construction": true});
            skLineSegment(sketch, "E56", {"start": v(-425, 7.63) * mm, "end": v(-170, 7.63) * mm, "construction": true});
            skLineSegment(sketch, "E57", {"start": v(-170, 7.63) * mm, "end": v(-170, -4.27) * mm, "construction": true});
            skCircle(sketch, "E58", {"center": v(-425, 0) * mm, "radius": 3.4 * mm});
            skCircle(sketch, "E59", {"center": v(-170, 0) * mm, "radius": 3.4 * mm});
            skLineSegment(sketch, "E60.MirrorCS", {"start": v(425, 0) * mm, "end": v(425, 7.63) * mm, "construction": true});
            skLineSegment(sketch, "E61.MirrorCS", {"start": v(170, 7.63) * mm, "end": v(170, -4.27) * mm, "construction": true});
            skCircle(sketch, "E62.MirrorC", {"center": v(425, 0) * mm, "radius": 3.4 * mm});
            skCircle(sketch, "E63.MirrorC", {"center": v(170, 0) * mm, "radius": 3.4 * mm});
            skSolve(sketch);
        }
        {
            var Q0;
            Q0 = qSketchRegion(id + "F15", true);
            extrude(context, id + "F16", {"entities" : qUnion([Q0]), "operationType" : NewBodyOperationType.REMOVE, "oppositeDirection" : true, "depth" : 25 * mm, "offsetDistance" : 25 * mm});
        }
        {
            var Q0;
            Q0=makeQuery(id+"F16.boolean.opBoolean","COPY",FACE,{"derivedFrom":makeQuery(id+"F16.opExtrude","SWEPT_FACE",FACE,{"disambiguationData":[OSD([sQuery(id+"F15.wireOp",EDGE,"E58")])]})});
            var Q1;
            Q1=makeQuery(id+"F16.boolean.opBoolean","COPY",FACE,{"derivedFrom":makeQuery(id+"F16.opExtrude","SWEPT_FACE",FACE,{"disambiguationData":[OSD([sQuery(id+"F15.wireOp",EDGE,"E59")])]})});
            var Q2;
            Q2=makeQuery(id+"F16.boolean.opBoolean","COPY",FACE,{"derivedFrom":makeQuery(id+"F16.opExtrude","SWEPT_FACE",FACE,{"disambiguationData":[OSD([sQuery(id+"F15.wireOp",EDGE,"E63.MirrorC")])]})});
            var Q3;
            Q3=makeQuery(id+"F16.boolean.opBoolean","COPY",FACE,{"derivedFrom":makeQuery(id+"F16.opExtrude","SWEPT_FACE",FACE,{"disambiguationData":[OSD([sQuery(id+"F15.wireOp",EDGE,"E62.MirrorC")])]})});
            chamfer(context, id + "F17", {"entities" : qUnion([Q0, Q1, Q2, Q3]), "width" : 0.5 * mm, "tangentPropagation" : true});
        }
        {
            var Q0;
            Q0=qCreatedBy(makeId("Front.planeOp"),FACE);
            var sketch = newSketch(context, id + "F18", { "sketchPlane" : qUnion([Q0])});
            skLineSegment(sketch, "E64", {"start": v(0, 0) * mm, "end": v(0, 118.84) * mm, "construction": true});
            skLineSegment(sketch, "E65", {"start": v(0, 118.84) * mm, "end": v(-340, 118.84) * mm, "construction": true});
            skLineSegment(sketch, "E66", {"start": v(-340, 118.84) * mm, "end": v(-340, -95.47) * mm, "construction": true});
            skLineSegment(sketch, "E67.0", {"start": v(-600, -9) * mm, "end": v(600, -9) * mm, "construction": true});
            skLineSegment(sketch, "E68", {"start": v(-340, -2) * mm, "end": v(-350, -2) * mm, "construction": true});
            skLineSegment(sketch, "E69", {"start": v(-350, -2) * mm, "end": v(-345.96, -9) * mm, "construction": true});
            skCircle(sketch, "E70.0", {"center": v(-367.5, 3) * mm, "radius": 3 * mm, "construction": true});
            skLineSegment(sketch, "E71.0", {"start": v(-297.5, 5) * mm, "end": v(-304.43, 9) * mm, "construction": true});
            skLineSegment(sketch, "E72.bottom", {"start": v(-315, -1) * mm, "end": v(-365, -1) * mm});
            skLineSegment(sketch, "E72.top", {"start": v(-315, 27.17) * mm, "end": v(-365, 27.17) * mm, "construction": true});
            skLineSegment(sketch, "E72.left", {"start": v(-315, -1) * mm, "end": v(-315, 27.17) * mm, "construction": true});
            skLineSegment(sketch, "E72.right", {"start": v(-365, -1) * mm, "end": v(-365, 27.17) * mm, "construction": true});
            skPoint(sketch, "E72.middle", {"position": v(-340, 13.09) * mm});
            skLineSegment(sketch, "E73.0", {"start": v(-375.57, 9) * mm, "end": v(-304.43, 9) * mm, "construction": true});
            skLineSegment(sketch, "E74", {"start": v(-365, -1) * mm, "end": v(-365, -18.59) * mm});
            skLineSegment(sketch, "E75", {"start": v(-365, -18.59) * mm, "end": v(-315, -18.59) * mm});
            skLineSegment(sketch, "E76", {"start": v(-315, -18.59) * mm, "end": v(-315, -1) * mm});
            skLineSegment(sketch, "E77.MirrorCS", {"start": v(365, -1) * mm, "end": v(365, -18.59) * mm});
            skLineSegment(sketch, "E78.MirrorCS", {"start": v(315, -1) * mm, "end": v(365, -1) * mm});
            skLineSegment(sketch, "E79.MirrorCS", {"start": v(365, -18.59) * mm, "end": v(315, -18.59) * mm});
            skLineSegment(sketch, "E80.MirrorCS", {"start": v(315, -18.59) * mm, "end": v(315, -1) * mm});
            skSolve(sketch);
        }
        {
            var Q0;
            Q0 = qSketchRegion(id + "F18", true);
            extrude(context, id + "F19", {"entities" : qUnion([Q0]), "operationType" : NewBodyOperationType.REMOVE, "endBound" : BoundingType.SYMMETRIC, "oppositeDirection" : true, "depth" : 50 * mm, "offsetDistance" : 25 * mm});
        }
        {
            var Q0;
            Q0=makeQuery(id+"F19.boolean.opBoolean","COPY",FACE,{"derivedFrom":makeQuery(id+"F19.opExtrude","SWEPT_FACE",FACE,{"disambiguationData":[OSD([sQuery(id+"F18.wireOp",EDGE,"E72.bottom")])]})});
            var sketch = newSketch(context, id + "F20", { "sketchPlane" : qUnion([Q0])});
            skLineSegment(sketch, "E81.0.0", {"start": v(-315, -12) * mm, "end": v(-315, 18) * mm, "construction": true});
            skLineSegment(sketch, "E81.0.1", {"start": v(-315, 18) * mm, "end": v(-365, 18) * mm, "construction": true});
            skLineSegment(sketch, "E81.0.2", {"start": v(-365, 18) * mm, "end": v(-365, -12) * mm, "construction": true});
            skLineSegment(sketch, "E81.0.3", {"start": v(-365, -12) * mm, "end": v(-315, -12) * mm, "construction": true});
            skLineSegment(sketch, "E82", {"start": v(-365, 18) * mm, "end": v(-315, -12) * mm, "construction": true});
            skLineSegment(sketch, "E83.bottom", {"start": v(-357.5, -7) * mm, "end": v(-322.5, -7) * mm, "construction": true});
            skLineSegment(sketch, "E83.top", {"start": v(-357.5, 13) * mm, "end": v(-322.5, 13) * mm, "construction": true});
            skLineSegment(sketch, "E83.left", {"start": v(-357.5, -7) * mm, "end": v(-357.5, 13) * mm, "construction": true});
            skLineSegment(sketch, "E83.right", {"start": v(-322.5, -7) * mm, "end": v(-322.5, 13) * mm, "construction": true});
            skPoint(sketch, "E83.middle", {"position": v(-340, 3) * mm});
            skCircle(sketch, "E84", {"center": v(-357.5, 13) * mm, "radius": 2.5 * mm});
            skCircle(sketch, "E85", {"center": v(-322.5, 13) * mm, "radius": 2.5 * mm});
            skCircle(sketch, "E86", {"center": v(-322.5, -7) * mm, "radius": 2.5 * mm});
            skCircle(sketch, "E87", {"center": v(-357.5, -7) * mm, "radius": 2.5 * mm});
            skLineSegment(sketch, "E88", {"start": v(0, 0) * mm, "end": v(0, -139.2) * mm, "construction": true});
            skCircle(sketch, "E89.MirrorC", {"center": v(322.5, 13) * mm, "radius": 2.5 * mm});
            skCircle(sketch, "E90.MirrorC", {"center": v(322.5, -7) * mm, "radius": 2.5 * mm});
            skCircle(sketch, "E91.MirrorC", {"center": v(357.5, 13) * mm, "radius": 2.5 * mm});
            skLineSegment(sketch, "E92.bottom", {"start": v(322.5, -7) * mm, "end": v(357.5, -7) * mm, "construction": true});
            skLineSegment(sketch, "E92.top", {"start": v(322.5, 13) * mm, "end": v(357.5, 13) * mm, "construction": true});
            skLineSegment(sketch, "E92.left", {"start": v(322.5, -7) * mm, "end": v(322.5, 13) * mm, "construction": true});
            skLineSegment(sketch, "E92.right", {"start": v(357.5, -7) * mm, "end": v(357.5, 13) * mm, "construction": true});
            skCircle(sketch, "E93", {"center": v(357.5, -7) * mm, "radius": 2.5 * mm});
            skSolve(sketch);
        }
        {
            var Q0;
            Q0 = qSketchRegion(id + "F20", true);
            extrude(context, id + "F21", {"entities" : qUnion([Q0]), "operationType" : NewBodyOperationType.REMOVE, "oppositeDirection" : true, "depth" : 25 * mm, "offsetDistance" : 25 * mm});
        }
        {
            var Q0;
            Q0=makeQuery(id+"F21.boolean.opBoolean","COPY",FACE,{"derivedFrom":makeQuery(id+"F21.opExtrude","SWEPT_FACE",FACE,{"disambiguationData":[OSD([sQuery(id+"F20.wireOp",EDGE,"E87")])]})});
            var Q1;
            Q1=makeQuery(id+"F21.boolean.opBoolean","COPY",FACE,{"derivedFrom":makeQuery(id+"F21.opExtrude","SWEPT_FACE",FACE,{"disambiguationData":[OSD([sQuery(id+"F20.wireOp",EDGE,"E84")])]})});
            var Q2;
            Q2=makeQuery(id+"F21.boolean.opBoolean","COPY",FACE,{"derivedFrom":makeQuery(id+"F21.opExtrude","SWEPT_FACE",FACE,{"disambiguationData":[OSD([sQuery(id+"F20.wireOp",EDGE,"E85")])]})});
            var Q3;
            Q3=makeQuery(id+"F21.boolean.opBoolean","COPY",FACE,{"derivedFrom":makeQuery(id+"F21.opExtrude","SWEPT_FACE",FACE,{"disambiguationData":[OSD([sQuery(id+"F20.wireOp",EDGE,"E86")])]})});
            var Q4;
            Q4=makeQuery(id+"F21.boolean.opBoolean","COPY",FACE,{"derivedFrom":makeQuery(id+"F21.opExtrude","SWEPT_FACE",FACE,{"disambiguationData":[OSD([sQuery(id+"F20.wireOp",EDGE,"E89.MirrorC")])]})});
            var Q5;
            Q5=makeQuery(id+"F21.boolean.opBoolean","COPY",FACE,{"derivedFrom":makeQuery(id+"F21.opExtrude","SWEPT_FACE",FACE,{"disambiguationData":[OSD([sQuery(id+"F20.wireOp",EDGE,"E90.MirrorC")])]})});
            var Q6;
            Q6=makeQuery(id+"F21.boolean.opBoolean","COPY",FACE,{"derivedFrom":makeQuery(id+"F21.opExtrude","SWEPT_FACE",FACE,{"disambiguationData":[OSD([sQuery(id+"F20.wireOp",EDGE,"E91.MirrorC")])]})});
            var Q7;
            Q7=makeQuery(id+"F21.boolean.opBoolean","COPY",FACE,{"derivedFrom":makeQuery(id+"F21.opExtrude","SWEPT_FACE",FACE,{"disambiguationData":[OSD([sQuery(id+"F20.wireOp",EDGE,"E90.MirrorC")])]})});
            var Q8;
            Q8=makeQuery(id+"F21.boolean.opBoolean","COPY",FACE,{"derivedFrom":makeQuery(id+"F21.opExtrude","SWEPT_FACE",FACE,{"disambiguationData":[OSD([sQuery(id+"F20.wireOp",EDGE,"E93")])]})});
            chamfer(context, id + "F22", {"entities" : qUnion([Q0, Q1, Q2, Q3, Q4, Q5, Q6, Q7, Q8]), "width" : 0.5 * mm, "tangentPropagation" : true});
        }
        {
            var Q0;
            Q0=makeQuery(id+"F19.boolean.opBoolean","INTERSECT",EDGE,{"derivedFrom":[makeQuery(id+"F1.opExtrude","CAP_FACE",FACE,{"disambiguationData":[OSD([sQuery(id+"F0.wireOp",EDGE,"E0.bottom"),sQuery(id+"F0.wireOp",EDGE,"E0.top"),sQuery(id+"F0.wireOp",EDGE,"E0.left"),sQuery(id+"F0.wireOp",EDGE,"E0.right"),sQuery(id+"F0.wireOp",EDGE,"E4"),sQuery(id+"F0.wireOp",EDGE,"E5.MirrorCS"),sQuery(id+"F0.wireOp",EDGE,"E6.1.0.0"),sQuery(id+"F0.wireOp",EDGE,"E6.1.0.1"),sQuery(id+"F0.wireOp",EDGE,"E6.2.0.0"),sQuery(id+"F0.wireOp",EDGE,"E6.2.0.1"),sQuery(id+"F0.wireOp",EDGE,"E6.3.0.0"),sQuery(id+"F0.wireOp",EDGE,"E6.3.0.1"),sQuery(id+"F0.wireOp",EDGE,"E6.4.0.0"),sQuery(id+"F0.wireOp",EDGE,"E6.4.0.1"),sQuery(id+"F0.wireOp",EDGE,"E6.5.0.0"),sQuery(id+"F0.wireOp",EDGE,"E6.5.0.1"),sQuery(id+"F0.wireOp",EDGE,"E6.6.0.0"),sQuery(id+"F0.wireOp",EDGE,"E6.6.0.1"),sQuery(id+"F0.wireOp",EDGE,"E6.7.0.0"),sQuery(id+"F0.wireOp",EDGE,"E6.7.0.1"),sQuery(id+"F0.wireOp",EDGE,"E6.8.0.0"),sQuery(id+"F0.wireOp",EDGE,"E6.8.0.1"),sQuery(id+"F0.wireOp",EDGE,"E6.9.0.0"),sQuery(id+"F0.wireOp",EDGE,"E6.9.0.1"),sQuery(id+"F0.wireOp",EDGE,"E6.10.0.0"),sQuery(id+"F0.wireOp",EDGE,"E6.10.0.1"),sQuery(id+"F0.wireOp",EDGE,"E6.11.0.0"),sQuery(id+"F0.wireOp",EDGE,"E6.11.0.1"),sQuery(id+"F0.wireOp",EDGE,"E6.12.0.0"),sQuery(id+"F0.wireOp",EDGE,"E6.12.0.1"),sQuery(id+"F0.wireOp",EDGE,"E6.13.0.0"),sQuery(id+"F0.wireOp",EDGE,"E6.13.0.1"),sQuery(id+"F0.wireOp",EDGE,"E8.trimOffspring"),sQuery(id+"F0.wireOp",EDGE,"E9.trimOffspring"),sQuery(id+"F0.wireOp",EDGE,"E10.trimOffspring"),sQuery(id+"F0.wireOp",EDGE,"E11.trimOffspring"),sQuery(id+"F0.wireOp",EDGE,"E12.trimOffspring"),sQuery(id+"F0.wireOp",EDGE,"E13.trimOffspring"),sQuery(id+"F0.wireOp",EDGE,"E14.trimOffspring"),sQuery(id+"F0.wireOp",EDGE,"E15.trimOffspring"),sQuery(id+"F0.wireOp",EDGE,"E16.trimOffspring"),sQuery(id+"F0.wireOp",EDGE,"E17.trimOffspring"),sQuery(id+"F0.wireOp",EDGE,"E18.trimOffspring"),sQuery(id+"F0.wireOp",EDGE,"E19.trimOffspring"),sQuery(id+"F0.wireOp",EDGE,"E20.trimOffspring"),sQuery(id+"F0.wireOp",EDGE,"E21.trimOffspring")])],"isStart":true}),makeQuery(id+"F19.opExtrude","SWEPT_FACE",FACE,{"disambiguationData":[OSD([sQuery(id+"F18.wireOp",EDGE,"E74")])]})]});
            var Q1;
            Q1=makeQuery(id+"F19.boolean.opBoolean","INTERSECT",EDGE,{"derivedFrom":[makeQuery(id+"F1.opExtrude","CAP_FACE",FACE,{"disambiguationData":[OSD([sQuery(id+"F0.wireOp",EDGE,"E0.bottom"),sQuery(id+"F0.wireOp",EDGE,"E0.top"),sQuery(id+"F0.wireOp",EDGE,"E0.left"),sQuery(id+"F0.wireOp",EDGE,"E0.right"),sQuery(id+"F0.wireOp",EDGE,"E4"),sQuery(id+"F0.wireOp",EDGE,"E5.MirrorCS"),sQuery(id+"F0.wireOp",EDGE,"E6.1.0.0"),sQuery(id+"F0.wireOp",EDGE,"E6.1.0.1"),sQuery(id+"F0.wireOp",EDGE,"E6.2.0.0"),sQuery(id+"F0.wireOp",EDGE,"E6.2.0.1"),sQuery(id+"F0.wireOp",EDGE,"E6.3.0.0"),sQuery(id+"F0.wireOp",EDGE,"E6.3.0.1"),sQuery(id+"F0.wireOp",EDGE,"E6.4.0.0"),sQuery(id+"F0.wireOp",EDGE,"E6.4.0.1"),sQuery(id+"F0.wireOp",EDGE,"E6.5.0.0"),sQuery(id+"F0.wireOp",EDGE,"E6.5.0.1"),sQuery(id+"F0.wireOp",EDGE,"E6.6.0.0"),sQuery(id+"F0.wireOp",EDGE,"E6.6.0.1"),sQuery(id+"F0.wireOp",EDGE,"E6.7.0.0"),sQuery(id+"F0.wireOp",EDGE,"E6.7.0.1"),sQuery(id+"F0.wireOp",EDGE,"E6.8.0.0"),sQuery(id+"F0.wireOp",EDGE,"E6.8.0.1"),sQuery(id+"F0.wireOp",EDGE,"E6.9.0.0"),sQuery(id+"F0.wireOp",EDGE,"E6.9.0.1"),sQuery(id+"F0.wireOp",EDGE,"E6.10.0.0"),sQuery(id+"F0.wireOp",EDGE,"E6.10.0.1"),sQuery(id+"F0.wireOp",EDGE,"E6.11.0.0"),sQuery(id+"F0.wireOp",EDGE,"E6.11.0.1"),sQuery(id+"F0.wireOp",EDGE,"E6.12.0.0"),sQuery(id+"F0.wireOp",EDGE,"E6.12.0.1"),sQuery(id+"F0.wireOp",EDGE,"E6.13.0.0"),sQuery(id+"F0.wireOp",EDGE,"E6.13.0.1"),sQuery(id+"F0.wireOp",EDGE,"E8.trimOffspring"),sQuery(id+"F0.wireOp",EDGE,"E9.trimOffspring"),sQuery(id+"F0.wireOp",EDGE,"E10.trimOffspring"),sQuery(id+"F0.wireOp",EDGE,"E11.trimOffspring"),sQuery(id+"F0.wireOp",EDGE,"E12.trimOffspring"),sQuery(id+"F0.wireOp",EDGE,"E13.trimOffspring"),sQuery(id+"F0.wireOp",EDGE,"E14.trimOffspring"),sQuery(id+"F0.wireOp",EDGE,"E15.trimOffspring"),sQuery(id+"F0.wireOp",EDGE,"E16.trimOffspring"),sQuery(id+"F0.wireOp",EDGE,"E17.trimOffspring"),sQuery(id+"F0.wireOp",EDGE,"E18.trimOffspring"),sQuery(id+"F0.wireOp",EDGE,"E19.trimOffspring"),sQuery(id+"F0.wireOp",EDGE,"E20.trimOffspring"),sQuery(id+"F0.wireOp",EDGE,"E21.trimOffspring")])],"isStart":true}),makeQuery(id+"F19.opExtrude","SWEPT_FACE",FACE,{"disambiguationData":[OSD([sQuery(id+"F18.wireOp",EDGE,"E72.bottom")])]})]});
            var Q2;
            Q2=makeQuery(id+"F19.boolean.opBoolean","INTERSECT",EDGE,{"derivedFrom":[makeQuery(id+"F1.opExtrude","CAP_FACE",FACE,{"disambiguationData":[OSD([sQuery(id+"F0.wireOp",EDGE,"E0.bottom"),sQuery(id+"F0.wireOp",EDGE,"E0.top"),sQuery(id+"F0.wireOp",EDGE,"E0.left"),sQuery(id+"F0.wireOp",EDGE,"E0.right"),sQuery(id+"F0.wireOp",EDGE,"E4"),sQuery(id+"F0.wireOp",EDGE,"E5.MirrorCS"),sQuery(id+"F0.wireOp",EDGE,"E6.1.0.0"),sQuery(id+"F0.wireOp",EDGE,"E6.1.0.1"),sQuery(id+"F0.wireOp",EDGE,"E6.2.0.0"),sQuery(id+"F0.wireOp",EDGE,"E6.2.0.1"),sQuery(id+"F0.wireOp",EDGE,"E6.3.0.0"),sQuery(id+"F0.wireOp",EDGE,"E6.3.0.1"),sQuery(id+"F0.wireOp",EDGE,"E6.4.0.0"),sQuery(id+"F0.wireOp",EDGE,"E6.4.0.1"),sQuery(id+"F0.wireOp",EDGE,"E6.5.0.0"),sQuery(id+"F0.wireOp",EDGE,"E6.5.0.1"),sQuery(id+"F0.wireOp",EDGE,"E6.6.0.0"),sQuery(id+"F0.wireOp",EDGE,"E6.6.0.1"),sQuery(id+"F0.wireOp",EDGE,"E6.7.0.0"),sQuery(id+"F0.wireOp",EDGE,"E6.7.0.1"),sQuery(id+"F0.wireOp",EDGE,"E6.8.0.0"),sQuery(id+"F0.wireOp",EDGE,"E6.8.0.1"),sQuery(id+"F0.wireOp",EDGE,"E6.9.0.0"),sQuery(id+"F0.wireOp",EDGE,"E6.9.0.1"),sQuery(id+"F0.wireOp",EDGE,"E6.10.0.0"),sQuery(id+"F0.wireOp",EDGE,"E6.10.0.1"),sQuery(id+"F0.wireOp",EDGE,"E6.11.0.0"),sQuery(id+"F0.wireOp",EDGE,"E6.11.0.1"),sQuery(id+"F0.wireOp",EDGE,"E6.12.0.0"),sQuery(id+"F0.wireOp",EDGE,"E6.12.0.1"),sQuery(id+"F0.wireOp",EDGE,"E6.13.0.0"),sQuery(id+"F0.wireOp",EDGE,"E6.13.0.1"),sQuery(id+"F0.wireOp",EDGE,"E8.trimOffspring"),sQuery(id+"F0.wireOp",EDGE,"E9.trimOffspring"),sQuery(id+"F0.wireOp",EDGE,"E10.trimOffspring"),sQuery(id+"F0.wireOp",EDGE,"E11.trimOffspring"),sQuery(id+"F0.wireOp",EDGE,"E12.trimOffspring"),sQuery(id+"F0.wireOp",EDGE,"E13.trimOffspring"),sQuery(id+"F0.wireOp",EDGE,"E14.trimOffspring"),sQuery(id+"F0.wireOp",EDGE,"E15.trimOffspring"),sQuery(id+"F0.wireOp",EDGE,"E16.trimOffspring"),sQuery(id+"F0.wireOp",EDGE,"E17.trimOffspring"),sQuery(id+"F0.wireOp",EDGE,"E18.trimOffspring"),sQuery(id+"F0.wireOp",EDGE,"E19.trimOffspring"),sQuery(id+"F0.wireOp",EDGE,"E20.trimOffspring"),sQuery(id+"F0.wireOp",EDGE,"E21.trimOffspring")])],"isStart":true}),makeQuery(id+"F19.opExtrude","SWEPT_FACE",FACE,{"disambiguationData":[OSD([sQuery(id+"F18.wireOp",EDGE,"E76")])]})]});
            var Q3;
            Q3=makeQuery(id+"F19.boolean.opBoolean","INTERSECT",EDGE,{"derivedFrom":[makeQuery(id+"F4.opExtrude","CAP_FACE",FACE,{"disambiguationData":[OSD([sQuery(id+"F0.wireOp",EDGE,"E0.bottom"),sQuery(id+"F0.wireOp",EDGE,"E0.top"),sQuery(id+"F0.wireOp",EDGE,"E0.left"),sQuery(id+"F0.wireOp",EDGE,"E0.right"),sQuery(id+"F0.wireOp",EDGE,"E4"),sQuery(id+"F0.wireOp",EDGE,"E5.MirrorCS"),sQuery(id+"F0.wireOp",EDGE,"E6.1.0.0"),sQuery(id+"F0.wireOp",EDGE,"E6.1.0.1"),sQuery(id+"F0.wireOp",EDGE,"E6.2.0.0"),sQuery(id+"F0.wireOp",EDGE,"E6.2.0.1"),sQuery(id+"F0.wireOp",EDGE,"E6.3.0.0"),sQuery(id+"F0.wireOp",EDGE,"E6.3.0.1"),sQuery(id+"F0.wireOp",EDGE,"E6.4.0.0"),sQuery(id+"F0.wireOp",EDGE,"E6.4.0.1"),sQuery(id+"F0.wireOp",EDGE,"E6.5.0.0"),sQuery(id+"F0.wireOp",EDGE,"E6.5.0.1"),sQuery(id+"F0.wireOp",EDGE,"E6.6.0.0"),sQuery(id+"F0.wireOp",EDGE,"E6.6.0.1"),sQuery(id+"F0.wireOp",EDGE,"E6.7.0.0"),sQuery(id+"F0.wireOp",EDGE,"E6.7.0.1"),sQuery(id+"F0.wireOp",EDGE,"E6.8.0.0"),sQuery(id+"F0.wireOp",EDGE,"E6.8.0.1"),sQuery(id+"F0.wireOp",EDGE,"E6.9.0.0"),sQuery(id+"F0.wireOp",EDGE,"E6.9.0.1"),sQuery(id+"F0.wireOp",EDGE,"E6.10.0.0"),sQuery(id+"F0.wireOp",EDGE,"E6.10.0.1"),sQuery(id+"F0.wireOp",EDGE,"E6.11.0.0"),sQuery(id+"F0.wireOp",EDGE,"E6.11.0.1"),sQuery(id+"F0.wireOp",EDGE,"E6.12.0.0"),sQuery(id+"F0.wireOp",EDGE,"E6.12.0.1"),sQuery(id+"F0.wireOp",EDGE,"E6.13.0.0"),sQuery(id+"F0.wireOp",EDGE,"E6.13.0.1"),sQuery(id+"F0.wireOp",EDGE,"E8.trimOffspring"),sQuery(id+"F0.wireOp",EDGE,"E9.trimOffspring"),sQuery(id+"F0.wireOp",EDGE,"E10.trimOffspring"),sQuery(id+"F0.wireOp",EDGE,"E11.trimOffspring"),sQuery(id+"F0.wireOp",EDGE,"E12.trimOffspring"),sQuery(id+"F0.wireOp",EDGE,"E13.trimOffspring"),sQuery(id+"F0.wireOp",EDGE,"E14.trimOffspring"),sQuery(id+"F0.wireOp",EDGE,"E15.trimOffspring"),sQuery(id+"F0.wireOp",EDGE,"E16.trimOffspring"),sQuery(id+"F0.wireOp",EDGE,"E17.trimOffspring"),sQuery(id+"F0.wireOp",EDGE,"E18.trimOffspring"),sQuery(id+"F0.wireOp",EDGE,"E19.trimOffspring"),sQuery(id+"F0.wireOp",EDGE,"E20.trimOffspring"),sQuery(id+"F0.wireOp",EDGE,"E21.trimOffspring")])],"isStart":false}),makeQuery(id+"F19.opExtrude","SWEPT_FACE",FACE,{"disambiguationData":[OSD([sQuery(id+"F18.wireOp",EDGE,"E76")])]})]});
            var Q4;
            Q4=makeQuery(id+"F19.boolean.opBoolean","INTERSECT",EDGE,{"derivedFrom":[makeQuery(id+"F4.opExtrude","CAP_FACE",FACE,{"disambiguationData":[OSD([sQuery(id+"F0.wireOp",EDGE,"E0.bottom"),sQuery(id+"F0.wireOp",EDGE,"E0.top"),sQuery(id+"F0.wireOp",EDGE,"E0.left"),sQuery(id+"F0.wireOp",EDGE,"E0.right"),sQuery(id+"F0.wireOp",EDGE,"E4"),sQuery(id+"F0.wireOp",EDGE,"E5.MirrorCS"),sQuery(id+"F0.wireOp",EDGE,"E6.1.0.0"),sQuery(id+"F0.wireOp",EDGE,"E6.1.0.1"),sQuery(id+"F0.wireOp",EDGE,"E6.2.0.0"),sQuery(id+"F0.wireOp",EDGE,"E6.2.0.1"),sQuery(id+"F0.wireOp",EDGE,"E6.3.0.0"),sQuery(id+"F0.wireOp",EDGE,"E6.3.0.1"),sQuery(id+"F0.wireOp",EDGE,"E6.4.0.0"),sQuery(id+"F0.wireOp",EDGE,"E6.4.0.1"),sQuery(id+"F0.wireOp",EDGE,"E6.5.0.0"),sQuery(id+"F0.wireOp",EDGE,"E6.5.0.1"),sQuery(id+"F0.wireOp",EDGE,"E6.6.0.0"),sQuery(id+"F0.wireOp",EDGE,"E6.6.0.1"),sQuery(id+"F0.wireOp",EDGE,"E6.7.0.0"),sQuery(id+"F0.wireOp",EDGE,"E6.7.0.1"),sQuery(id+"F0.wireOp",EDGE,"E6.8.0.0"),sQuery(id+"F0.wireOp",EDGE,"E6.8.0.1"),sQuery(id+"F0.wireOp",EDGE,"E6.9.0.0"),sQuery(id+"F0.wireOp",EDGE,"E6.9.0.1"),sQuery(id+"F0.wireOp",EDGE,"E6.10.0.0"),sQuery(id+"F0.wireOp",EDGE,"E6.10.0.1"),sQuery(id+"F0.wireOp",EDGE,"E6.11.0.0"),sQuery(id+"F0.wireOp",EDGE,"E6.11.0.1"),sQuery(id+"F0.wireOp",EDGE,"E6.12.0.0"),sQuery(id+"F0.wireOp",EDGE,"E6.12.0.1"),sQuery(id+"F0.wireOp",EDGE,"E6.13.0.0"),sQuery(id+"F0.wireOp",EDGE,"E6.13.0.1"),sQuery(id+"F0.wireOp",EDGE,"E8.trimOffspring"),sQuery(id+"F0.wireOp",EDGE,"E9.trimOffspring"),sQuery(id+"F0.wireOp",EDGE,"E10.trimOffspring"),sQuery(id+"F0.wireOp",EDGE,"E11.trimOffspring"),sQuery(id+"F0.wireOp",EDGE,"E12.trimOffspring"),sQuery(id+"F0.wireOp",EDGE,"E13.trimOffspring"),sQuery(id+"F0.wireOp",EDGE,"E14.trimOffspring"),sQuery(id+"F0.wireOp",EDGE,"E15.trimOffspring"),sQuery(id+"F0.wireOp",EDGE,"E16.trimOffspring"),sQuery(id+"F0.wireOp",EDGE,"E17.trimOffspring"),sQuery(id+"F0.wireOp",EDGE,"E18.trimOffspring"),sQuery(id+"F0.wireOp",EDGE,"E19.trimOffspring"),sQuery(id+"F0.wireOp",EDGE,"E20.trimOffspring"),sQuery(id+"F0.wireOp",EDGE,"E21.trimOffspring")])],"isStart":false}),makeQuery(id+"F19.opExtrude","SWEPT_FACE",FACE,{"disambiguationData":[OSD([sQuery(id+"F18.wireOp",EDGE,"E72.bottom")])]})]});
            var Q5;
            Q5=makeQuery(id+"F19.boolean.opBoolean","INTERSECT",EDGE,{"derivedFrom":[makeQuery(id+"F4.opExtrude","CAP_FACE",FACE,{"disambiguationData":[OSD([sQuery(id+"F0.wireOp",EDGE,"E0.bottom"),sQuery(id+"F0.wireOp",EDGE,"E0.top"),sQuery(id+"F0.wireOp",EDGE,"E0.left"),sQuery(id+"F0.wireOp",EDGE,"E0.right"),sQuery(id+"F0.wireOp",EDGE,"E4"),sQuery(id+"F0.wireOp",EDGE,"E5.MirrorCS"),sQuery(id+"F0.wireOp",EDGE,"E6.1.0.0"),sQuery(id+"F0.wireOp",EDGE,"E6.1.0.1"),sQuery(id+"F0.wireOp",EDGE,"E6.2.0.0"),sQuery(id+"F0.wireOp",EDGE,"E6.2.0.1"),sQuery(id+"F0.wireOp",EDGE,"E6.3.0.0"),sQuery(id+"F0.wireOp",EDGE,"E6.3.0.1"),sQuery(id+"F0.wireOp",EDGE,"E6.4.0.0"),sQuery(id+"F0.wireOp",EDGE,"E6.4.0.1"),sQuery(id+"F0.wireOp",EDGE,"E6.5.0.0"),sQuery(id+"F0.wireOp",EDGE,"E6.5.0.1"),sQuery(id+"F0.wireOp",EDGE,"E6.6.0.0"),sQuery(id+"F0.wireOp",EDGE,"E6.6.0.1"),sQuery(id+"F0.wireOp",EDGE,"E6.7.0.0"),sQuery(id+"F0.wireOp",EDGE,"E6.7.0.1"),sQuery(id+"F0.wireOp",EDGE,"E6.8.0.0"),sQuery(id+"F0.wireOp",EDGE,"E6.8.0.1"),sQuery(id+"F0.wireOp",EDGE,"E6.9.0.0"),sQuery(id+"F0.wireOp",EDGE,"E6.9.0.1"),sQuery(id+"F0.wireOp",EDGE,"E6.10.0.0"),sQuery(id+"F0.wireOp",EDGE,"E6.10.0.1"),sQuery(id+"F0.wireOp",EDGE,"E6.11.0.0"),sQuery(id+"F0.wireOp",EDGE,"E6.11.0.1"),sQuery(id+"F0.wireOp",EDGE,"E6.12.0.0"),sQuery(id+"F0.wireOp",EDGE,"E6.12.0.1"),sQuery(id+"F0.wireOp",EDGE,"E6.13.0.0"),sQuery(id+"F0.wireOp",EDGE,"E6.13.0.1"),sQuery(id+"F0.wireOp",EDGE,"E8.trimOffspring"),sQuery(id+"F0.wireOp",EDGE,"E9.trimOffspring"),sQuery(id+"F0.wireOp",EDGE,"E10.trimOffspring"),sQuery(id+"F0.wireOp",EDGE,"E11.trimOffspring"),sQuery(id+"F0.wireOp",EDGE,"E12.trimOffspring"),sQuery(id+"F0.wireOp",EDGE,"E13.trimOffspring"),sQuery(id+"F0.wireOp",EDGE,"E14.trimOffspring"),sQuery(id+"F0.wireOp",EDGE,"E15.trimOffspring"),sQuery(id+"F0.wireOp",EDGE,"E16.trimOffspring"),sQuery(id+"F0.wireOp",EDGE,"E17.trimOffspring"),sQuery(id+"F0.wireOp",EDGE,"E18.trimOffspring"),sQuery(id+"F0.wireOp",EDGE,"E19.trimOffspring"),sQuery(id+"F0.wireOp",EDGE,"E20.trimOffspring"),sQuery(id+"F0.wireOp",EDGE,"E21.trimOffspring")])],"isStart":false}),makeQuery(id+"F19.opExtrude","SWEPT_FACE",FACE,{"disambiguationData":[OSD([sQuery(id+"F18.wireOp",EDGE,"E74")])]})]});
            var Q6;
            Q6=makeQuery(id+"F19.boolean.opBoolean","INTERSECT",EDGE,{"derivedFrom":[makeQuery(id+"F1.opExtrude","CAP_FACE",FACE,{"disambiguationData":[OSD([sQuery(id+"F0.wireOp",EDGE,"E0.bottom"),sQuery(id+"F0.wireOp",EDGE,"E0.top"),sQuery(id+"F0.wireOp",EDGE,"E0.left"),sQuery(id+"F0.wireOp",EDGE,"E0.right"),sQuery(id+"F0.wireOp",EDGE,"E4"),sQuery(id+"F0.wireOp",EDGE,"E5.MirrorCS"),sQuery(id+"F0.wireOp",EDGE,"E6.1.0.0"),sQuery(id+"F0.wireOp",EDGE,"E6.1.0.1"),sQuery(id+"F0.wireOp",EDGE,"E6.2.0.0"),sQuery(id+"F0.wireOp",EDGE,"E6.2.0.1"),sQuery(id+"F0.wireOp",EDGE,"E6.3.0.0"),sQuery(id+"F0.wireOp",EDGE,"E6.3.0.1"),sQuery(id+"F0.wireOp",EDGE,"E6.4.0.0"),sQuery(id+"F0.wireOp",EDGE,"E6.4.0.1"),sQuery(id+"F0.wireOp",EDGE,"E6.5.0.0"),sQuery(id+"F0.wireOp",EDGE,"E6.5.0.1"),sQuery(id+"F0.wireOp",EDGE,"E6.6.0.0"),sQuery(id+"F0.wireOp",EDGE,"E6.6.0.1"),sQuery(id+"F0.wireOp",EDGE,"E6.7.0.0"),sQuery(id+"F0.wireOp",EDGE,"E6.7.0.1"),sQuery(id+"F0.wireOp",EDGE,"E6.8.0.0"),sQuery(id+"F0.wireOp",EDGE,"E6.8.0.1"),sQuery(id+"F0.wireOp",EDGE,"E6.9.0.0"),sQuery(id+"F0.wireOp",EDGE,"E6.9.0.1"),sQuery(id+"F0.wireOp",EDGE,"E6.10.0.0"),sQuery(id+"F0.wireOp",EDGE,"E6.10.0.1"),sQuery(id+"F0.wireOp",EDGE,"E6.11.0.0"),sQuery(id+"F0.wireOp",EDGE,"E6.11.0.1"),sQuery(id+"F0.wireOp",EDGE,"E6.12.0.0"),sQuery(id+"F0.wireOp",EDGE,"E6.12.0.1"),sQuery(id+"F0.wireOp",EDGE,"E6.13.0.0"),sQuery(id+"F0.wireOp",EDGE,"E6.13.0.1"),sQuery(id+"F0.wireOp",EDGE,"E8.trimOffspring"),sQuery(id+"F0.wireOp",EDGE,"E9.trimOffspring"),sQuery(id+"F0.wireOp",EDGE,"E10.trimOffspring"),sQuery(id+"F0.wireOp",EDGE,"E11.trimOffspring"),sQuery(id+"F0.wireOp",EDGE,"E12.trimOffspring"),sQuery(id+"F0.wireOp",EDGE,"E13.trimOffspring"),sQuery(id+"F0.wireOp",EDGE,"E14.trimOffspring"),sQuery(id+"F0.wireOp",EDGE,"E15.trimOffspring"),sQuery(id+"F0.wireOp",EDGE,"E16.trimOffspring"),sQuery(id+"F0.wireOp",EDGE,"E17.trimOffspring"),sQuery(id+"F0.wireOp",EDGE,"E18.trimOffspring"),sQuery(id+"F0.wireOp",EDGE,"E19.trimOffspring"),sQuery(id+"F0.wireOp",EDGE,"E20.trimOffspring"),sQuery(id+"F0.wireOp",EDGE,"E21.trimOffspring")])],"isStart":true}),makeQuery(id+"F19.opExtrude","SWEPT_FACE",FACE,{"disambiguationData":[OSD([sQuery(id+"F18.wireOp",EDGE,"E80.MirrorCS")])]})]});
            var Q7;
            Q7=makeQuery(id+"F19.boolean.opBoolean","INTERSECT",EDGE,{"derivedFrom":[makeQuery(id+"F4.opExtrude","CAP_FACE",FACE,{"disambiguationData":[OSD([sQuery(id+"F0.wireOp",EDGE,"E0.bottom"),sQuery(id+"F0.wireOp",EDGE,"E0.top"),sQuery(id+"F0.wireOp",EDGE,"E0.left"),sQuery(id+"F0.wireOp",EDGE,"E0.right"),sQuery(id+"F0.wireOp",EDGE,"E4"),sQuery(id+"F0.wireOp",EDGE,"E5.MirrorCS"),sQuery(id+"F0.wireOp",EDGE,"E6.1.0.0"),sQuery(id+"F0.wireOp",EDGE,"E6.1.0.1"),sQuery(id+"F0.wireOp",EDGE,"E6.2.0.0"),sQuery(id+"F0.wireOp",EDGE,"E6.2.0.1"),sQuery(id+"F0.wireOp",EDGE,"E6.3.0.0"),sQuery(id+"F0.wireOp",EDGE,"E6.3.0.1"),sQuery(id+"F0.wireOp",EDGE,"E6.4.0.0"),sQuery(id+"F0.wireOp",EDGE,"E6.4.0.1"),sQuery(id+"F0.wireOp",EDGE,"E6.5.0.0"),sQuery(id+"F0.wireOp",EDGE,"E6.5.0.1"),sQuery(id+"F0.wireOp",EDGE,"E6.6.0.0"),sQuery(id+"F0.wireOp",EDGE,"E6.6.0.1"),sQuery(id+"F0.wireOp",EDGE,"E6.7.0.0"),sQuery(id+"F0.wireOp",EDGE,"E6.7.0.1"),sQuery(id+"F0.wireOp",EDGE,"E6.8.0.0"),sQuery(id+"F0.wireOp",EDGE,"E6.8.0.1"),sQuery(id+"F0.wireOp",EDGE,"E6.9.0.0"),sQuery(id+"F0.wireOp",EDGE,"E6.9.0.1"),sQuery(id+"F0.wireOp",EDGE,"E6.10.0.0"),sQuery(id+"F0.wireOp",EDGE,"E6.10.0.1"),sQuery(id+"F0.wireOp",EDGE,"E6.11.0.0"),sQuery(id+"F0.wireOp",EDGE,"E6.11.0.1"),sQuery(id+"F0.wireOp",EDGE,"E6.12.0.0"),sQuery(id+"F0.wireOp",EDGE,"E6.12.0.1"),sQuery(id+"F0.wireOp",EDGE,"E6.13.0.0"),sQuery(id+"F0.wireOp",EDGE,"E6.13.0.1"),sQuery(id+"F0.wireOp",EDGE,"E8.trimOffspring"),sQuery(id+"F0.wireOp",EDGE,"E9.trimOffspring"),sQuery(id+"F0.wireOp",EDGE,"E10.trimOffspring"),sQuery(id+"F0.wireOp",EDGE,"E11.trimOffspring"),sQuery(id+"F0.wireOp",EDGE,"E12.trimOffspring"),sQuery(id+"F0.wireOp",EDGE,"E13.trimOffspring"),sQuery(id+"F0.wireOp",EDGE,"E14.trimOffspring"),sQuery(id+"F0.wireOp",EDGE,"E15.trimOffspring"),sQuery(id+"F0.wireOp",EDGE,"E16.trimOffspring"),sQuery(id+"F0.wireOp",EDGE,"E17.trimOffspring"),sQuery(id+"F0.wireOp",EDGE,"E18.trimOffspring"),sQuery(id+"F0.wireOp",EDGE,"E19.trimOffspring"),sQuery(id+"F0.wireOp",EDGE,"E20.trimOffspring"),sQuery(id+"F0.wireOp",EDGE,"E21.trimOffspring")])],"isStart":false}),makeQuery(id+"F19.opExtrude","SWEPT_FACE",FACE,{"disambiguationData":[OSD([sQuery(id+"F18.wireOp",EDGE,"E80.MirrorCS")])]})]});
            var Q8;
            Q8=makeQuery(id+"F19.boolean.opBoolean","INTERSECT",EDGE,{"derivedFrom":[makeQuery(id+"F4.opExtrude","CAP_FACE",FACE,{"disambiguationData":[OSD([sQuery(id+"F0.wireOp",EDGE,"E0.bottom"),sQuery(id+"F0.wireOp",EDGE,"E0.top"),sQuery(id+"F0.wireOp",EDGE,"E0.left"),sQuery(id+"F0.wireOp",EDGE,"E0.right"),sQuery(id+"F0.wireOp",EDGE,"E4"),sQuery(id+"F0.wireOp",EDGE,"E5.MirrorCS"),sQuery(id+"F0.wireOp",EDGE,"E6.1.0.0"),sQuery(id+"F0.wireOp",EDGE,"E6.1.0.1"),sQuery(id+"F0.wireOp",EDGE,"E6.2.0.0"),sQuery(id+"F0.wireOp",EDGE,"E6.2.0.1"),sQuery(id+"F0.wireOp",EDGE,"E6.3.0.0"),sQuery(id+"F0.wireOp",EDGE,"E6.3.0.1"),sQuery(id+"F0.wireOp",EDGE,"E6.4.0.0"),sQuery(id+"F0.wireOp",EDGE,"E6.4.0.1"),sQuery(id+"F0.wireOp",EDGE,"E6.5.0.0"),sQuery(id+"F0.wireOp",EDGE,"E6.5.0.1"),sQuery(id+"F0.wireOp",EDGE,"E6.6.0.0"),sQuery(id+"F0.wireOp",EDGE,"E6.6.0.1"),sQuery(id+"F0.wireOp",EDGE,"E6.7.0.0"),sQuery(id+"F0.wireOp",EDGE,"E6.7.0.1"),sQuery(id+"F0.wireOp",EDGE,"E6.8.0.0"),sQuery(id+"F0.wireOp",EDGE,"E6.8.0.1"),sQuery(id+"F0.wireOp",EDGE,"E6.9.0.0"),sQuery(id+"F0.wireOp",EDGE,"E6.9.0.1"),sQuery(id+"F0.wireOp",EDGE,"E6.10.0.0"),sQuery(id+"F0.wireOp",EDGE,"E6.10.0.1"),sQuery(id+"F0.wireOp",EDGE,"E6.11.0.0"),sQuery(id+"F0.wireOp",EDGE,"E6.11.0.1"),sQuery(id+"F0.wireOp",EDGE,"E6.12.0.0"),sQuery(id+"F0.wireOp",EDGE,"E6.12.0.1"),sQuery(id+"F0.wireOp",EDGE,"E6.13.0.0"),sQuery(id+"F0.wireOp",EDGE,"E6.13.0.1"),sQuery(id+"F0.wireOp",EDGE,"E8.trimOffspring"),sQuery(id+"F0.wireOp",EDGE,"E9.trimOffspring"),sQuery(id+"F0.wireOp",EDGE,"E10.trimOffspring"),sQuery(id+"F0.wireOp",EDGE,"E11.trimOffspring"),sQuery(id+"F0.wireOp",EDGE,"E12.trimOffspring"),sQuery(id+"F0.wireOp",EDGE,"E13.trimOffspring"),sQuery(id+"F0.wireOp",EDGE,"E14.trimOffspring"),sQuery(id+"F0.wireOp",EDGE,"E15.trimOffspring"),sQuery(id+"F0.wireOp",EDGE,"E16.trimOffspring"),sQuery(id+"F0.wireOp",EDGE,"E17.trimOffspring"),sQuery(id+"F0.wireOp",EDGE,"E18.trimOffspring"),sQuery(id+"F0.wireOp",EDGE,"E19.trimOffspring"),sQuery(id+"F0.wireOp",EDGE,"E20.trimOffspring"),sQuery(id+"F0.wireOp",EDGE,"E21.trimOffspring")])],"isStart":false}),makeQuery(id+"F19.opExtrude","SWEPT_FACE",FACE,{"disambiguationData":[OSD([sQuery(id+"F18.wireOp",EDGE,"E78.MirrorCS")])]})]});
            var Q9;
            Q9=makeQuery(id+"F19.boolean.opBoolean","INTERSECT",EDGE,{"derivedFrom":[makeQuery(id+"F1.opExtrude","CAP_FACE",FACE,{"disambiguationData":[OSD([sQuery(id+"F0.wireOp",EDGE,"E0.bottom"),sQuery(id+"F0.wireOp",EDGE,"E0.top"),sQuery(id+"F0.wireOp",EDGE,"E0.left"),sQuery(id+"F0.wireOp",EDGE,"E0.right"),sQuery(id+"F0.wireOp",EDGE,"E4"),sQuery(id+"F0.wireOp",EDGE,"E5.MirrorCS"),sQuery(id+"F0.wireOp",EDGE,"E6.1.0.0"),sQuery(id+"F0.wireOp",EDGE,"E6.1.0.1"),sQuery(id+"F0.wireOp",EDGE,"E6.2.0.0"),sQuery(id+"F0.wireOp",EDGE,"E6.2.0.1"),sQuery(id+"F0.wireOp",EDGE,"E6.3.0.0"),sQuery(id+"F0.wireOp",EDGE,"E6.3.0.1"),sQuery(id+"F0.wireOp",EDGE,"E6.4.0.0"),sQuery(id+"F0.wireOp",EDGE,"E6.4.0.1"),sQuery(id+"F0.wireOp",EDGE,"E6.5.0.0"),sQuery(id+"F0.wireOp",EDGE,"E6.5.0.1"),sQuery(id+"F0.wireOp",EDGE,"E6.6.0.0"),sQuery(id+"F0.wireOp",EDGE,"E6.6.0.1"),sQuery(id+"F0.wireOp",EDGE,"E6.7.0.0"),sQuery(id+"F0.wireOp",EDGE,"E6.7.0.1"),sQuery(id+"F0.wireOp",EDGE,"E6.8.0.0"),sQuery(id+"F0.wireOp",EDGE,"E6.8.0.1"),sQuery(id+"F0.wireOp",EDGE,"E6.9.0.0"),sQuery(id+"F0.wireOp",EDGE,"E6.9.0.1"),sQuery(id+"F0.wireOp",EDGE,"E6.10.0.0"),sQuery(id+"F0.wireOp",EDGE,"E6.10.0.1"),sQuery(id+"F0.wireOp",EDGE,"E6.11.0.0"),sQuery(id+"F0.wireOp",EDGE,"E6.11.0.1"),sQuery(id+"F0.wireOp",EDGE,"E6.12.0.0"),sQuery(id+"F0.wireOp",EDGE,"E6.12.0.1"),sQuery(id+"F0.wireOp",EDGE,"E6.13.0.0"),sQuery(id+"F0.wireOp",EDGE,"E6.13.0.1"),sQuery(id+"F0.wireOp",EDGE,"E8.trimOffspring"),sQuery(id+"F0.wireOp",EDGE,"E9.trimOffspring"),sQuery(id+"F0.wireOp",EDGE,"E10.trimOffspring"),sQuery(id+"F0.wireOp",EDGE,"E11.trimOffspring"),sQuery(id+"F0.wireOp",EDGE,"E12.trimOffspring"),sQuery(id+"F0.wireOp",EDGE,"E13.trimOffspring"),sQuery(id+"F0.wireOp",EDGE,"E14.trimOffspring"),sQuery(id+"F0.wireOp",EDGE,"E15.trimOffspring"),sQuery(id+"F0.wireOp",EDGE,"E16.trimOffspring"),sQuery(id+"F0.wireOp",EDGE,"E17.trimOffspring"),sQuery(id+"F0.wireOp",EDGE,"E18.trimOffspring"),sQuery(id+"F0.wireOp",EDGE,"E19.trimOffspring"),sQuery(id+"F0.wireOp",EDGE,"E20.trimOffspring"),sQuery(id+"F0.wireOp",EDGE,"E21.trimOffspring")])],"isStart":true}),makeQuery(id+"F19.opExtrude","SWEPT_FACE",FACE,{"disambiguationData":[OSD([sQuery(id+"F18.wireOp",EDGE,"E78.MirrorCS")])]})]});
            var Q10;
            Q10=makeQuery(id+"F19.boolean.opBoolean","INTERSECT",EDGE,{"derivedFrom":[makeQuery(id+"F1.opExtrude","CAP_FACE",FACE,{"disambiguationData":[OSD([sQuery(id+"F0.wireOp",EDGE,"E0.bottom"),sQuery(id+"F0.wireOp",EDGE,"E0.top"),sQuery(id+"F0.wireOp",EDGE,"E0.left"),sQuery(id+"F0.wireOp",EDGE,"E0.right"),sQuery(id+"F0.wireOp",EDGE,"E4"),sQuery(id+"F0.wireOp",EDGE,"E5.MirrorCS"),sQuery(id+"F0.wireOp",EDGE,"E6.1.0.0"),sQuery(id+"F0.wireOp",EDGE,"E6.1.0.1"),sQuery(id+"F0.wireOp",EDGE,"E6.2.0.0"),sQuery(id+"F0.wireOp",EDGE,"E6.2.0.1"),sQuery(id+"F0.wireOp",EDGE,"E6.3.0.0"),sQuery(id+"F0.wireOp",EDGE,"E6.3.0.1"),sQuery(id+"F0.wireOp",EDGE,"E6.4.0.0"),sQuery(id+"F0.wireOp",EDGE,"E6.4.0.1"),sQuery(id+"F0.wireOp",EDGE,"E6.5.0.0"),sQuery(id+"F0.wireOp",EDGE,"E6.5.0.1"),sQuery(id+"F0.wireOp",EDGE,"E6.6.0.0"),sQuery(id+"F0.wireOp",EDGE,"E6.6.0.1"),sQuery(id+"F0.wireOp",EDGE,"E6.7.0.0"),sQuery(id+"F0.wireOp",EDGE,"E6.7.0.1"),sQuery(id+"F0.wireOp",EDGE,"E6.8.0.0"),sQuery(id+"F0.wireOp",EDGE,"E6.8.0.1"),sQuery(id+"F0.wireOp",EDGE,"E6.9.0.0"),sQuery(id+"F0.wireOp",EDGE,"E6.9.0.1"),sQuery(id+"F0.wireOp",EDGE,"E6.10.0.0"),sQuery(id+"F0.wireOp",EDGE,"E6.10.0.1"),sQuery(id+"F0.wireOp",EDGE,"E6.11.0.0"),sQuery(id+"F0.wireOp",EDGE,"E6.11.0.1"),sQuery(id+"F0.wireOp",EDGE,"E6.12.0.0"),sQuery(id+"F0.wireOp",EDGE,"E6.12.0.1"),sQuery(id+"F0.wireOp",EDGE,"E6.13.0.0"),sQuery(id+"F0.wireOp",EDGE,"E6.13.0.1"),sQuery(id+"F0.wireOp",EDGE,"E8.trimOffspring"),sQuery(id+"F0.wireOp",EDGE,"E9.trimOffspring"),sQuery(id+"F0.wireOp",EDGE,"E10.trimOffspring"),sQuery(id+"F0.wireOp",EDGE,"E11.trimOffspring"),sQuery(id+"F0.wireOp",EDGE,"E12.trimOffspring"),sQuery(id+"F0.wireOp",EDGE,"E13.trimOffspring"),sQuery(id+"F0.wireOp",EDGE,"E14.trimOffspring"),sQuery(id+"F0.wireOp",EDGE,"E15.trimOffspring"),sQuery(id+"F0.wireOp",EDGE,"E16.trimOffspring"),sQuery(id+"F0.wireOp",EDGE,"E17.trimOffspring"),sQuery(id+"F0.wireOp",EDGE,"E18.trimOffspring"),sQuery(id+"F0.wireOp",EDGE,"E19.trimOffspring"),sQuery(id+"F0.wireOp",EDGE,"E20.trimOffspring"),sQuery(id+"F0.wireOp",EDGE,"E21.trimOffspring")])],"isStart":true}),makeQuery(id+"F19.opExtrude","SWEPT_FACE",FACE,{"disambiguationData":[OSD([sQuery(id+"F18.wireOp",EDGE,"E77.MirrorCS")])]})]});
            var Q11;
            Q11=makeQuery(id+"F19.boolean.opBoolean","INTERSECT",EDGE,{"derivedFrom":[makeQuery(id+"F4.opExtrude","CAP_FACE",FACE,{"disambiguationData":[OSD([sQuery(id+"F0.wireOp",EDGE,"E0.bottom"),sQuery(id+"F0.wireOp",EDGE,"E0.top"),sQuery(id+"F0.wireOp",EDGE,"E0.left"),sQuery(id+"F0.wireOp",EDGE,"E0.right"),sQuery(id+"F0.wireOp",EDGE,"E4"),sQuery(id+"F0.wireOp",EDGE,"E5.MirrorCS"),sQuery(id+"F0.wireOp",EDGE,"E6.1.0.0"),sQuery(id+"F0.wireOp",EDGE,"E6.1.0.1"),sQuery(id+"F0.wireOp",EDGE,"E6.2.0.0"),sQuery(id+"F0.wireOp",EDGE,"E6.2.0.1"),sQuery(id+"F0.wireOp",EDGE,"E6.3.0.0"),sQuery(id+"F0.wireOp",EDGE,"E6.3.0.1"),sQuery(id+"F0.wireOp",EDGE,"E6.4.0.0"),sQuery(id+"F0.wireOp",EDGE,"E6.4.0.1"),sQuery(id+"F0.wireOp",EDGE,"E6.5.0.0"),sQuery(id+"F0.wireOp",EDGE,"E6.5.0.1"),sQuery(id+"F0.wireOp",EDGE,"E6.6.0.0"),sQuery(id+"F0.wireOp",EDGE,"E6.6.0.1"),sQuery(id+"F0.wireOp",EDGE,"E6.7.0.0"),sQuery(id+"F0.wireOp",EDGE,"E6.7.0.1"),sQuery(id+"F0.wireOp",EDGE,"E6.8.0.0"),sQuery(id+"F0.wireOp",EDGE,"E6.8.0.1"),sQuery(id+"F0.wireOp",EDGE,"E6.9.0.0"),sQuery(id+"F0.wireOp",EDGE,"E6.9.0.1"),sQuery(id+"F0.wireOp",EDGE,"E6.10.0.0"),sQuery(id+"F0.wireOp",EDGE,"E6.10.0.1"),sQuery(id+"F0.wireOp",EDGE,"E6.11.0.0"),sQuery(id+"F0.wireOp",EDGE,"E6.11.0.1"),sQuery(id+"F0.wireOp",EDGE,"E6.12.0.0"),sQuery(id+"F0.wireOp",EDGE,"E6.12.0.1"),sQuery(id+"F0.wireOp",EDGE,"E6.13.0.0"),sQuery(id+"F0.wireOp",EDGE,"E6.13.0.1"),sQuery(id+"F0.wireOp",EDGE,"E8.trimOffspring"),sQuery(id+"F0.wireOp",EDGE,"E9.trimOffspring"),sQuery(id+"F0.wireOp",EDGE,"E10.trimOffspring"),sQuery(id+"F0.wireOp",EDGE,"E11.trimOffspring"),sQuery(id+"F0.wireOp",EDGE,"E12.trimOffspring"),sQuery(id+"F0.wireOp",EDGE,"E13.trimOffspring"),sQuery(id+"F0.wireOp",EDGE,"E14.trimOffspring"),sQuery(id+"F0.wireOp",EDGE,"E15.trimOffspring"),sQuery(id+"F0.wireOp",EDGE,"E16.trimOffspring"),sQuery(id+"F0.wireOp",EDGE,"E17.trimOffspring"),sQuery(id+"F0.wireOp",EDGE,"E18.trimOffspring"),sQuery(id+"F0.wireOp",EDGE,"E19.trimOffspring"),sQuery(id+"F0.wireOp",EDGE,"E20.trimOffspring"),sQuery(id+"F0.wireOp",EDGE,"E21.trimOffspring")])],"isStart":false}),makeQuery(id+"F19.opExtrude","SWEPT_FACE",FACE,{"disambiguationData":[OSD([sQuery(id+"F18.wireOp",EDGE,"E77.MirrorCS")])]})]});
            chamfer(context, id + "F23", {"entities" : qUnion([Q0, Q1, Q2, Q3, Q4, Q5, Q6, Q7, Q8, Q9, Q10, Q11]), "width" : 0.5 * mm});
        }
    });
